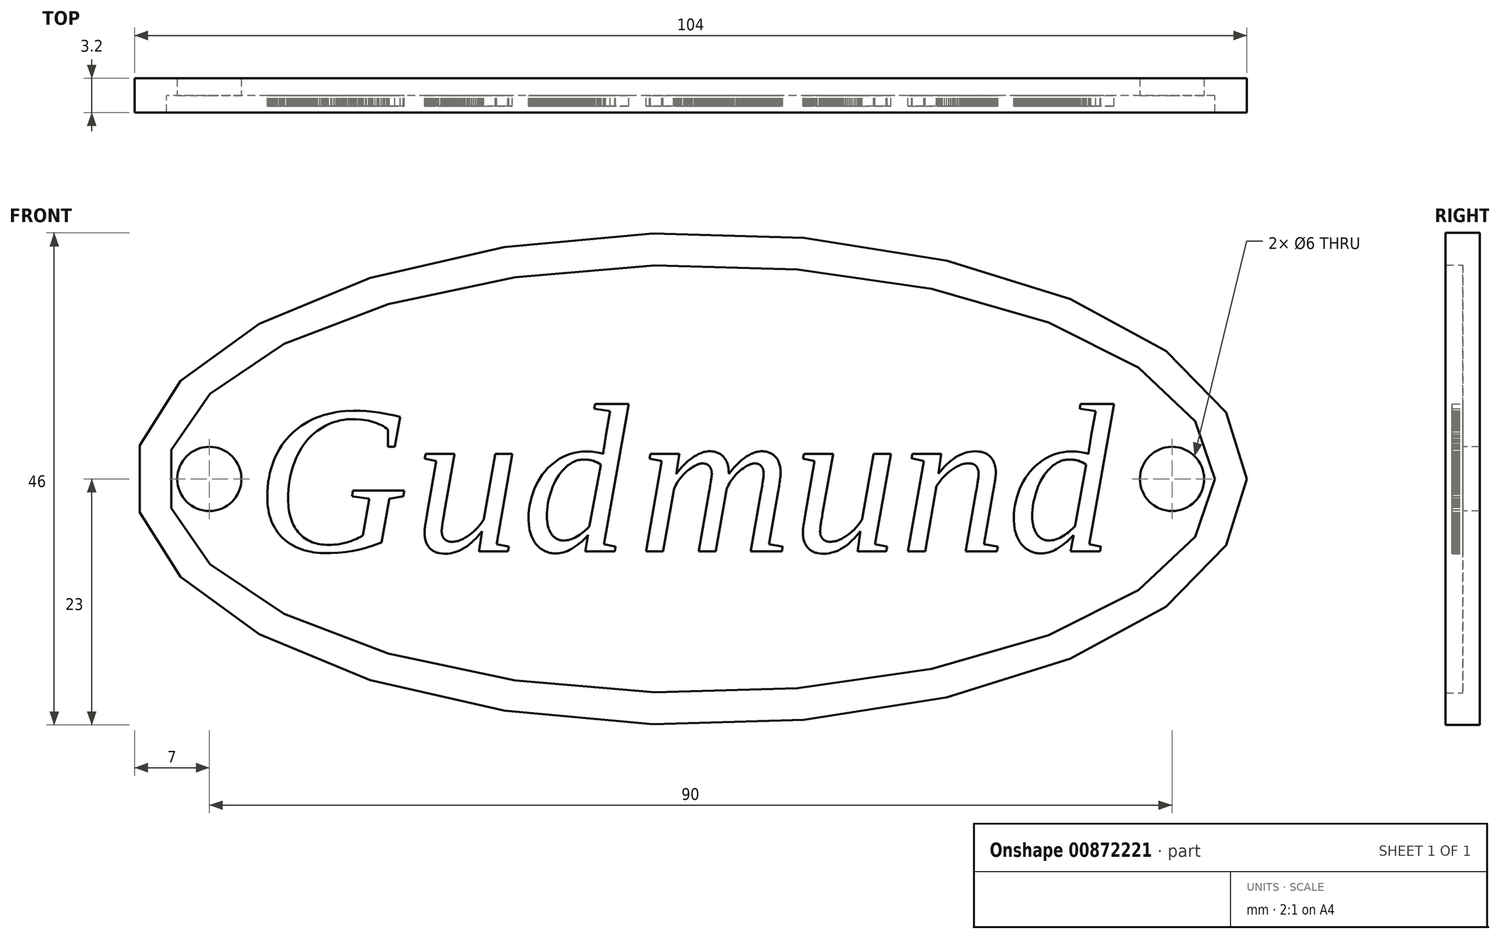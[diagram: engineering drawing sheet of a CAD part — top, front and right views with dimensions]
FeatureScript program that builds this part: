
annotation { "Feature Type Name" : "Feature", "Feature Type Description" : "" }
export const myFeature = defineFeature(function(context is Context, id is Id, definition is map)
    precondition{}
    {
        {
            var Q0;
            Q0=qCreatedBy(makeId("Front.planeOp"),FACE);
            var sketch = newSketch(context, id + "F0", { "sketchPlane" : qUnion([Q0])});
            skEllipse(sketch, "E0", {"center": v(0, 0) * mm, "majorRadius": 49 * mm, "minorRadius": 20 * mm, "majorAxis": v(1, 0)});
            skEllipse(sketch, "E1", {"center": v(0, 0) * mm, "majorRadius": 52 * mm, "minorRadius": 23 * mm, "majorAxis": v(1, 0)});
            skLineSegment(sketch, "E2", {"start": v(-81.12, 0) * mm, "end": v(85, 0) * mm, "construction": true});
            skPoint(sketch, "E2.startSnap0", {"position": v(-52, 0) * mm});
            skPoint(sketch, "E2.endSnap0", {"position": v(52, 0) * mm});
            skCircle(sketch, "E3", {"center": v(-45, 0) * mm, "radius": 3 * mm});
            skCircle(sketch, "E4", {"center": v(45, 0) * mm, "radius": 3 * mm});
            skLineSegment(sketch, "E5", {"start": v(-28.9, -5.93) * mm, "end": v(-29.2, -6.05) * mm});
            skLineSegment(sketch, "E6", {"start": v(-29.2, -6.05) * mm, "end": v(-29.8, -6.26) * mm});
            skLineSegment(sketch, "E7", {"start": v(-29.8, -6.26) * mm, "end": v(-30.1, -6.36) * mm});
            skLineSegment(sketch, "E8", {"start": v(-30.1, -6.36) * mm, "end": v(-30.4, -6.45) * mm});
            skLineSegment(sketch, "E9", {"start": v(-30.4, -6.45) * mm, "end": v(-31, -6.6) * mm});
            skLineSegment(sketch, "E10", {"start": v(-31, -6.6) * mm, "end": v(-31.3, -6.68) * mm});
            skLineSegment(sketch, "E11", {"start": v(-31.3, -6.68) * mm, "end": v(-31.62, -6.74) * mm});
            skLineSegment(sketch, "E12", {"start": v(-31.62, -6.74) * mm, "end": v(-32.26, -6.84) * mm});
            skLineSegment(sketch, "E13", {"start": v(-32.26, -6.84) * mm, "end": v(-32.6, -6.87) * mm});
            skLineSegment(sketch, "E14", {"start": v(-32.6, -6.87) * mm, "end": v(-32.93, -6.9) * mm});
            skLineSegment(sketch, "E15", {"start": v(-32.93, -6.9) * mm, "end": v(-33.63, -6.94) * mm});
            skLineSegment(sketch, "E16", {"start": v(-33.63, -6.94) * mm, "end": v(-33.99, -6.94) * mm});
            skLineSegment(sketch, "E17", {"start": v(-33.99, -6.94) * mm, "end": v(-34.32, -6.94) * mm});
            skLineSegment(sketch, "E18", {"start": v(-34.32, -6.94) * mm, "end": v(-34.64, -6.92) * mm});
            skLineSegment(sketch, "E19", {"start": v(-34.64, -6.92) * mm, "end": v(-34.95, -6.9) * mm});
            skLineSegment(sketch, "E20", {"start": v(-34.95, -6.9) * mm, "end": v(-35.25, -6.85) * mm});
            skLineSegment(sketch, "E21", {"start": v(-35.25, -6.85) * mm, "end": v(-35.55, -6.8) * mm});
            skLineSegment(sketch, "E22", {"start": v(-35.55, -6.8) * mm, "end": v(-35.83, -6.74) * mm});
            skLineSegment(sketch, "E23", {"start": v(-35.83, -6.74) * mm, "end": v(-36.1, -6.67) * mm});
            skLineSegment(sketch, "E24", {"start": v(-36.1, -6.67) * mm, "end": v(-36.37, -6.58) * mm});
            skLineSegment(sketch, "E25", {"start": v(-36.37, -6.58) * mm, "end": v(-36.63, -6.49) * mm});
            skLineSegment(sketch, "E26", {"start": v(-36.63, -6.49) * mm, "end": v(-36.87, -6.38) * mm});
            skLineSegment(sketch, "E27", {"start": v(-36.87, -6.38) * mm, "end": v(-37.1, -6.26) * mm});
            skLineSegment(sketch, "E28", {"start": v(-37.1, -6.26) * mm, "end": v(-37.33, -6.14) * mm});
            skLineSegment(sketch, "E29", {"start": v(-37.33, -6.14) * mm, "end": v(-37.54, -6) * mm});
            skLineSegment(sketch, "E30", {"start": v(-37.54, -6) * mm, "end": v(-37.75, -5.86) * mm});
            skLineSegment(sketch, "E31", {"start": v(-37.75, -5.86) * mm, "end": v(-37.94, -5.7) * mm});
            skLineSegment(sketch, "E32", {"start": v(-37.94, -5.7) * mm, "end": v(-38.13, -5.54) * mm});
            skLineSegment(sketch, "E33", {"start": v(-38.13, -5.54) * mm, "end": v(-38.3, -5.36) * mm});
            skLineSegment(sketch, "E34", {"start": v(-38.3, -5.36) * mm, "end": v(-38.46, -5.18) * mm});
            skLineSegment(sketch, "E35", {"start": v(-38.46, -5.18) * mm, "end": v(-38.61, -4.99) * mm});
            skLineSegment(sketch, "E36", {"start": v(-38.61, -4.99) * mm, "end": v(-38.75, -4.79) * mm});
            skLineSegment(sketch, "E37", {"start": v(-38.75, -4.79) * mm, "end": v(-38.88, -4.58) * mm});
            skLineSegment(sketch, "E38", {"start": v(-38.88, -4.58) * mm, "end": v(-39, -4.36) * mm});
            skLineSegment(sketch, "E39", {"start": v(-39, -4.36) * mm, "end": v(-39.11, -4.13) * mm});
            skLineSegment(sketch, "E40", {"start": v(-39.11, -4.13) * mm, "end": v(-39.21, -3.9) * mm});
            skLineSegment(sketch, "E41", {"start": v(-39.21, -3.9) * mm, "end": v(-39.3, -3.64) * mm});
            skLineSegment(sketch, "E42", {"start": v(-39.3, -3.64) * mm, "end": v(-39.37, -3.39) * mm});
            skLineSegment(sketch, "E43", {"start": v(-39.37, -3.39) * mm, "end": v(-39.44, -3.13) * mm});
            skLineSegment(sketch, "E44", {"start": v(-39.44, -3.13) * mm, "end": v(-39.49, -2.86) * mm});
            skLineSegment(sketch, "E45", {"start": v(-39.49, -2.86) * mm, "end": v(-39.53, -2.58) * mm});
            skLineSegment(sketch, "E46", {"start": v(-39.53, -2.58) * mm, "end": v(-39.56, -2.3) * mm});
            skLineSegment(sketch, "E47", {"start": v(-39.56, -2.3) * mm, "end": v(-39.57, -2) * mm});
            skLineSegment(sketch, "E48", {"start": v(-39.57, -2) * mm, "end": v(-39.58, -1.7) * mm});
            skLineSegment(sketch, "E49", {"start": v(-39.58, -1.7) * mm, "end": v(-39.57, -1.22) * mm});
            skLineSegment(sketch, "E50", {"start": v(-39.57, -1.22) * mm, "end": v(-39.54, -0.75) * mm});
            skLineSegment(sketch, "E51", {"start": v(-39.54, -0.75) * mm, "end": v(-39.5, -0.3) * mm});
            skLineSegment(sketch, "E52", {"start": v(-39.5, -0.3) * mm, "end": v(-39.42, 0.14) * mm});
            skLineSegment(sketch, "E53", {"start": v(-39.42, 0.14) * mm, "end": v(-39.34, 0.56) * mm});
            skLineSegment(sketch, "E54", {"start": v(-39.34, 0.56) * mm, "end": v(-39.23, 0.97) * mm});
            skLineSegment(sketch, "E55", {"start": v(-39.23, 0.97) * mm, "end": v(-39.1, 1.37) * mm});
            skLineSegment(sketch, "E56", {"start": v(-39.1, 1.37) * mm, "end": v(-38.96, 1.75) * mm});
            skLineSegment(sketch, "E57", {"start": v(-38.96, 1.75) * mm, "end": v(-38.8, 2.12) * mm});
            skLineSegment(sketch, "E58", {"start": v(-38.8, 2.12) * mm, "end": v(-38.62, 2.47) * mm});
            skLineSegment(sketch, "E59", {"start": v(-38.62, 2.47) * mm, "end": v(-38.43, 2.8) * mm});
            skLineSegment(sketch, "E60", {"start": v(-38.43, 2.8) * mm, "end": v(-38.22, 3.13) * mm});
            skLineSegment(sketch, "E61", {"start": v(-38.22, 3.13) * mm, "end": v(-38, 3.44) * mm});
            skLineSegment(sketch, "E62", {"start": v(-38, 3.44) * mm, "end": v(-37.77, 3.73) * mm});
            skLineSegment(sketch, "E63", {"start": v(-37.77, 3.73) * mm, "end": v(-37.52, 4.01) * mm});
            skLineSegment(sketch, "E64", {"start": v(-37.52, 4.01) * mm, "end": v(-37.25, 4.28) * mm});
            skLineSegment(sketch, "E65", {"start": v(-37.25, 4.28) * mm, "end": v(-36.98, 4.53) * mm});
            skLineSegment(sketch, "E66", {"start": v(-36.98, 4.53) * mm, "end": v(-36.69, 4.76) * mm});
            skLineSegment(sketch, "E67", {"start": v(-36.69, 4.76) * mm, "end": v(-36.39, 4.98) * mm});
            skLineSegment(sketch, "E68", {"start": v(-36.39, 4.98) * mm, "end": v(-36.07, 5.18) * mm});
            skLineSegment(sketch, "E69", {"start": v(-36.07, 5.18) * mm, "end": v(-35.75, 5.37) * mm});
            skLineSegment(sketch, "E70", {"start": v(-35.75, 5.37) * mm, "end": v(-35.4, 5.54) * mm});
            skLineSegment(sketch, "E71", {"start": v(-35.4, 5.54) * mm, "end": v(-35.06, 5.7) * mm});
            skLineSegment(sketch, "E72", {"start": v(-35.06, 5.7) * mm, "end": v(-34.7, 5.84) * mm});
            skLineSegment(sketch, "E73", {"start": v(-34.7, 5.84) * mm, "end": v(-34.32, 5.96) * mm});
            skLineSegment(sketch, "E74", {"start": v(-34.32, 5.96) * mm, "end": v(-33.94, 6.07) * mm});
            skLineSegment(sketch, "E75", {"start": v(-33.94, 6.07) * mm, "end": v(-33.55, 6.16) * mm});
            skLineSegment(sketch, "E76", {"start": v(-33.55, 6.16) * mm, "end": v(-33.16, 6.24) * mm});
            skLineSegment(sketch, "E77", {"start": v(-33.16, 6.24) * mm, "end": v(-32.75, 6.3) * mm});
            skLineSegment(sketch, "E78", {"start": v(-32.75, 6.3) * mm, "end": v(-32.34, 6.34) * mm});
            skLineSegment(sketch, "E79", {"start": v(-32.34, 6.34) * mm, "end": v(-31.5, 6.37) * mm});
            skLineSegment(sketch, "E80", {"start": v(-31.5, 6.37) * mm, "end": v(-30.89, 6.36) * mm});
            skLineSegment(sketch, "E81", {"start": v(-30.89, 6.36) * mm, "end": v(-30.3, 6.33) * mm});
            skLineSegment(sketch, "E82", {"start": v(-30.3, 6.33) * mm, "end": v(-29.74, 6.28) * mm});
            skLineSegment(sketch, "E83", {"start": v(-29.74, 6.28) * mm, "end": v(-29.2, 6.22) * mm});
            skLineSegment(sketch, "E84", {"start": v(-29.2, 6.22) * mm, "end": v(-28.68, 6.13) * mm});
            skLineSegment(sketch, "E85", {"start": v(-28.68, 6.13) * mm, "end": v(-27.66, 5.92) * mm});
            skLineSegment(sketch, "E86", {"start": v(-27.66, 5.92) * mm, "end": v(-27.17, 5.79) * mm});
            skLineSegment(sketch, "E87", {"start": v(-27.17, 5.79) * mm, "end": v(-27.66, 3) * mm});
            skLineSegment(sketch, "E88", {"start": v(-27.66, 3) * mm, "end": v(-28.31, 3) * mm});
            skLineSegment(sketch, "E89", {"start": v(-28.31, 3) * mm, "end": v(-28.28, 4.6) * mm});
            skLineSegment(sketch, "E90", {"start": v(-28.28, 4.6) * mm, "end": v(-28.43, 4.72) * mm});
            skLineSegment(sketch, "E91", {"start": v(-28.43, 4.72) * mm, "end": v(-28.6, 4.83) * mm});
            skLineSegment(sketch, "E92", {"start": v(-28.6, 4.83) * mm, "end": v(-28.76, 4.93) * mm});
            skLineSegment(sketch, "E93", {"start": v(-28.76, 4.93) * mm, "end": v(-28.93, 5.03) * mm});
            skLineSegment(sketch, "E94", {"start": v(-28.93, 5.03) * mm, "end": v(-29.11, 5.11) * mm});
            skLineSegment(sketch, "E95", {"start": v(-29.11, 5.11) * mm, "end": v(-29.3, 5.2) * mm});
            skLineSegment(sketch, "E96", {"start": v(-29.3, 5.2) * mm, "end": v(-29.5, 5.27) * mm});
            skLineSegment(sketch, "E97", {"start": v(-29.5, 5.27) * mm, "end": v(-29.7, 5.33) * mm});
            skLineSegment(sketch, "E98", {"start": v(-29.7, 5.33) * mm, "end": v(-29.9, 5.4) * mm});
            skLineSegment(sketch, "E99", {"start": v(-29.9, 5.4) * mm, "end": v(-30.12, 5.45) * mm});
            skLineSegment(sketch, "E100", {"start": v(-30.12, 5.45) * mm, "end": v(-30.34, 5.5) * mm});
            skLineSegment(sketch, "E101", {"start": v(-30.34, 5.5) * mm, "end": v(-30.57, 5.53) * mm});
            skLineSegment(sketch, "E102", {"start": v(-30.57, 5.53) * mm, "end": v(-30.8, 5.56) * mm});
            skLineSegment(sketch, "E103", {"start": v(-30.8, 5.56) * mm, "end": v(-31.3, 5.6) * mm});
            skLineSegment(sketch, "E104", {"start": v(-31.3, 5.6) * mm, "end": v(-31.56, 5.6) * mm});
            skLineSegment(sketch, "E105", {"start": v(-31.56, 5.6) * mm, "end": v(-31.86, 5.59) * mm});
            skLineSegment(sketch, "E106", {"start": v(-31.86, 5.59) * mm, "end": v(-32.16, 5.56) * mm});
            skLineSegment(sketch, "E107", {"start": v(-32.16, 5.56) * mm, "end": v(-32.45, 5.53) * mm});
            skLineSegment(sketch, "E108", {"start": v(-32.45, 5.53) * mm, "end": v(-32.74, 5.47) * mm});
            skLineSegment(sketch, "E109", {"start": v(-32.74, 5.47) * mm, "end": v(-33.03, 5.4) * mm});
            skLineSegment(sketch, "E110", {"start": v(-33.03, 5.4) * mm, "end": v(-33.31, 5.32) * mm});
            skLineSegment(sketch, "E111", {"start": v(-33.31, 5.32) * mm, "end": v(-33.6, 5.22) * mm});
            skLineSegment(sketch, "E112", {"start": v(-33.6, 5.22) * mm, "end": v(-33.87, 5.1) * mm});
            skLineSegment(sketch, "E113", {"start": v(-33.87, 5.1) * mm, "end": v(-34.14, 4.97) * mm});
            skLineSegment(sketch, "E114", {"start": v(-34.14, 4.97) * mm, "end": v(-34.4, 4.83) * mm});
            skLineSegment(sketch, "E115", {"start": v(-34.4, 4.83) * mm, "end": v(-34.66, 4.67) * mm});
            skLineSegment(sketch, "E116", {"start": v(-34.66, 4.67) * mm, "end": v(-34.9, 4.5) * mm});
            skLineSegment(sketch, "E117", {"start": v(-34.9, 4.5) * mm, "end": v(-35.15, 4.31) * mm});
            skLineSegment(sketch, "E118", {"start": v(-35.15, 4.31) * mm, "end": v(-35.38, 4.11) * mm});
            skLineSegment(sketch, "E119", {"start": v(-35.38, 4.11) * mm, "end": v(-35.6, 3.9) * mm});
            skLineSegment(sketch, "E120", {"start": v(-35.6, 3.9) * mm, "end": v(-35.81, 3.67) * mm});
            skLineSegment(sketch, "E121", {"start": v(-35.81, 3.67) * mm, "end": v(-36.01, 3.42) * mm});
            skLineSegment(sketch, "E122", {"start": v(-36.01, 3.42) * mm, "end": v(-36.2, 3.16) * mm});
            skLineSegment(sketch, "E123", {"start": v(-36.2, 3.16) * mm, "end": v(-36.39, 2.9) * mm});
            skLineSegment(sketch, "E124", {"start": v(-36.39, 2.9) * mm, "end": v(-36.56, 2.6) * mm});
            skLineSegment(sketch, "E125", {"start": v(-36.56, 2.6) * mm, "end": v(-36.72, 2.3) * mm});
            skLineSegment(sketch, "E126", {"start": v(-36.72, 2.3) * mm, "end": v(-36.87, 1.99) * mm});
            skLineSegment(sketch, "E127", {"start": v(-36.87, 1.99) * mm, "end": v(-37, 1.66) * mm});
            skLineSegment(sketch, "E128", {"start": v(-37, 1.66) * mm, "end": v(-37.14, 1.31) * mm});
            skLineSegment(sketch, "E129", {"start": v(-37.14, 1.31) * mm, "end": v(-37.25, 0.96) * mm});
            skLineSegment(sketch, "E130", {"start": v(-37.25, 0.96) * mm, "end": v(-37.35, 0.59) * mm});
            skLineSegment(sketch, "E131", {"start": v(-37.35, 0.59) * mm, "end": v(-37.44, 0.2) * mm});
            skLineSegment(sketch, "E132", {"start": v(-37.44, 0.2) * mm, "end": v(-37.5, -0.19) * mm});
            skLineSegment(sketch, "E133", {"start": v(-37.5, -0.19) * mm, "end": v(-37.56, -0.6) * mm});
            skLineSegment(sketch, "E134", {"start": v(-37.56, -0.6) * mm, "end": v(-37.6, -1.01) * mm});
            skLineSegment(sketch, "E135", {"start": v(-37.6, -1.01) * mm, "end": v(-37.62, -1.45) * mm});
            skLineSegment(sketch, "E136", {"start": v(-37.62, -1.45) * mm, "end": v(-37.63, -1.9) * mm});
            skLineSegment(sketch, "E137", {"start": v(-37.63, -1.9) * mm, "end": v(-37.63, -2.16) * mm});
            skLineSegment(sketch, "E138", {"start": v(-37.63, -2.16) * mm, "end": v(-37.61, -2.41) * mm});
            skLineSegment(sketch, "E139", {"start": v(-37.61, -2.41) * mm, "end": v(-37.6, -2.66) * mm});
            skLineSegment(sketch, "E140", {"start": v(-37.6, -2.66) * mm, "end": v(-37.56, -2.9) * mm});
            skLineSegment(sketch, "E141", {"start": v(-37.56, -2.9) * mm, "end": v(-37.53, -3.12) * mm});
            skLineSegment(sketch, "E142", {"start": v(-37.53, -3.12) * mm, "end": v(-37.48, -3.35) * mm});
            skLineSegment(sketch, "E143", {"start": v(-37.48, -3.35) * mm, "end": v(-37.42, -3.56) * mm});
            skLineSegment(sketch, "E144", {"start": v(-37.42, -3.56) * mm, "end": v(-37.36, -3.76) * mm});
            skLineSegment(sketch, "E145", {"start": v(-37.36, -3.76) * mm, "end": v(-37.29, -3.96) * mm});
            skLineSegment(sketch, "E146", {"start": v(-37.29, -3.96) * mm, "end": v(-37.2, -4.15) * mm});
            skLineSegment(sketch, "E147", {"start": v(-37.2, -4.15) * mm, "end": v(-37.12, -4.33) * mm});
            skLineSegment(sketch, "E148", {"start": v(-37.12, -4.33) * mm, "end": v(-37.03, -4.5) * mm});
            skLineSegment(sketch, "E149", {"start": v(-37.03, -4.5) * mm, "end": v(-36.93, -4.66) * mm});
            skLineSegment(sketch, "E150", {"start": v(-36.93, -4.66) * mm, "end": v(-36.82, -4.82) * mm});
            skLineSegment(sketch, "E151", {"start": v(-36.82, -4.82) * mm, "end": v(-36.7, -4.96) * mm});
            skLineSegment(sketch, "E152", {"start": v(-36.7, -4.96) * mm, "end": v(-36.59, -5.1) * mm});
            skLineSegment(sketch, "E153", {"start": v(-36.59, -5.1) * mm, "end": v(-36.46, -5.23) * mm});
            skLineSegment(sketch, "E154", {"start": v(-36.46, -5.23) * mm, "end": v(-36.33, -5.35) * mm});
            skLineSegment(sketch, "E155", {"start": v(-36.33, -5.35) * mm, "end": v(-36.19, -5.46) * mm});
            skLineSegment(sketch, "E156", {"start": v(-36.19, -5.46) * mm, "end": v(-36.04, -5.57) * mm});
            skLineSegment(sketch, "E157", {"start": v(-36.04, -5.57) * mm, "end": v(-35.9, -5.67) * mm});
            skLineSegment(sketch, "E158", {"start": v(-35.9, -5.67) * mm, "end": v(-35.74, -5.75) * mm});
            skLineSegment(sketch, "E159", {"start": v(-35.74, -5.75) * mm, "end": v(-35.57, -5.83) * mm});
            skLineSegment(sketch, "E160", {"start": v(-35.57, -5.83) * mm, "end": v(-35.4, -5.9) * mm});
            skLineSegment(sketch, "E161", {"start": v(-35.4, -5.9) * mm, "end": v(-35.23, -5.97) * mm});
            skLineSegment(sketch, "E162", {"start": v(-35.23, -5.97) * mm, "end": v(-35.05, -6.02) * mm});
            skLineSegment(sketch, "E163", {"start": v(-35.05, -6.02) * mm, "end": v(-34.86, -6.06) * mm});
            skLineSegment(sketch, "E164", {"start": v(-34.86, -6.06) * mm, "end": v(-34.67, -6.1) * mm});
            skLineSegment(sketch, "E165", {"start": v(-34.67, -6.1) * mm, "end": v(-34.47, -6.13) * mm});
            skLineSegment(sketch, "E166", {"start": v(-34.47, -6.13) * mm, "end": v(-34.28, -6.15) * mm});
            skLineSegment(sketch, "E167", {"start": v(-34.28, -6.15) * mm, "end": v(-34.07, -6.16) * mm});
            skLineSegment(sketch, "E168", {"start": v(-34.07, -6.16) * mm, "end": v(-33.86, -6.17) * mm});
            skLineSegment(sketch, "E169", {"start": v(-33.86, -6.17) * mm, "end": v(-33.6, -6.16) * mm});
            skLineSegment(sketch, "E170", {"start": v(-33.6, -6.16) * mm, "end": v(-33.35, -6.15) * mm});
            skLineSegment(sketch, "E171", {"start": v(-33.35, -6.15) * mm, "end": v(-33.1, -6.12) * mm});
            skLineSegment(sketch, "E172", {"start": v(-33.1, -6.12) * mm, "end": v(-32.87, -6.09) * mm});
            skLineSegment(sketch, "E173", {"start": v(-32.87, -6.09) * mm, "end": v(-32.63, -6.04) * mm});
            skLineSegment(sketch, "E174", {"start": v(-32.63, -6.04) * mm, "end": v(-32.19, -5.94) * mm});
            skLineSegment(sketch, "E175", {"start": v(-32.19, -5.94) * mm, "end": v(-31.97, -5.88) * mm});
            skLineSegment(sketch, "E176", {"start": v(-31.97, -5.88) * mm, "end": v(-31.77, -5.8) * mm});
            skLineSegment(sketch, "E177", {"start": v(-31.77, -5.8) * mm, "end": v(-31.58, -5.74) * mm});
            skLineSegment(sketch, "E178", {"start": v(-31.58, -5.74) * mm, "end": v(-31.4, -5.66) * mm});
            skLineSegment(sketch, "E179", {"start": v(-31.4, -5.66) * mm, "end": v(-31.22, -5.59) * mm});
            skLineSegment(sketch, "E180", {"start": v(-31.22, -5.59) * mm, "end": v(-31.06, -5.5) * mm});
            skLineSegment(sketch, "E181", {"start": v(-31.06, -5.5) * mm, "end": v(-30.9, -5.43) * mm});
            skLineSegment(sketch, "E182", {"start": v(-30.9, -5.43) * mm, "end": v(-30.77, -5.36) * mm});
            skLineSegment(sketch, "E183", {"start": v(-30.77, -5.36) * mm, "end": v(-30.7, -5.32) * mm});
            skLineSegment(sketch, "E184", {"start": v(-30.7, -5.32) * mm, "end": v(-30.65, -5.29) * mm});
            skLineSegment(sketch, "E185", {"start": v(-30.65, -5.29) * mm, "end": v(-30.04, -1.87) * mm});
            skLineSegment(sketch, "E186", {"start": v(-30.04, -1.87) * mm, "end": v(-31.65, -1.61) * mm});
            skLineSegment(sketch, "E187", {"start": v(-31.65, -1.61) * mm, "end": v(-31.57, -1.09) * mm});
            skLineSegment(sketch, "E188", {"start": v(-31.57, -1.09) * mm, "end": v(-26.77, -1.09) * mm});
            skLineSegment(sketch, "E189", {"start": v(-26.77, -1.09) * mm, "end": v(-26.86, -1.61) * mm});
            skLineSegment(sketch, "E190", {"start": v(-26.86, -1.61) * mm, "end": v(-28.18, -1.87) * mm});
            skLineSegment(sketch, "E191", {"start": v(-28.18, -1.87) * mm, "end": v(-28.9, -5.93) * mm});
            skLineSegment(sketch, "E192", {"start": v(-23.27, -4.9) * mm, "end": v(-23.27, -5) * mm});
            skLineSegment(sketch, "E193", {"start": v(-23.27, -5) * mm, "end": v(-23.26, -5.06) * mm});
            skLineSegment(sketch, "E194", {"start": v(-23.26, -5.06) * mm, "end": v(-23.26, -5.1) * mm});
            skLineSegment(sketch, "E195", {"start": v(-23.26, -5.1) * mm, "end": v(-23.25, -5.15) * mm});
            skLineSegment(sketch, "E196", {"start": v(-23.25, -5.15) * mm, "end": v(-23.24, -5.2) * mm});
            skLineSegment(sketch, "E197", {"start": v(-23.24, -5.2) * mm, "end": v(-23.23, -5.25) * mm});
            skLineSegment(sketch, "E198", {"start": v(-23.23, -5.25) * mm, "end": v(-23.21, -5.3) * mm});
            skLineSegment(sketch, "E199", {"start": v(-23.21, -5.3) * mm, "end": v(-23.2, -5.34) * mm});
            skLineSegment(sketch, "E200", {"start": v(-23.2, -5.34) * mm, "end": v(-23.18, -5.38) * mm});
            skLineSegment(sketch, "E201", {"start": v(-23.18, -5.38) * mm, "end": v(-23.16, -5.42) * mm});
            skLineSegment(sketch, "E202", {"start": v(-23.16, -5.42) * mm, "end": v(-23.14, -5.46) * mm});
            skLineSegment(sketch, "E203", {"start": v(-23.14, -5.46) * mm, "end": v(-23.12, -5.5) * mm});
            skLineSegment(sketch, "E204", {"start": v(-23.12, -5.5) * mm, "end": v(-23.1, -5.53) * mm});
            skLineSegment(sketch, "E205", {"start": v(-23.1, -5.53) * mm, "end": v(-23.07, -5.57) * mm});
            skLineSegment(sketch, "E206", {"start": v(-23.07, -5.57) * mm, "end": v(-23.04, -5.6) * mm});
            skLineSegment(sketch, "E207", {"start": v(-23.04, -5.6) * mm, "end": v(-23.01, -5.64) * mm});
            skLineSegment(sketch, "E208", {"start": v(-23.01, -5.64) * mm, "end": v(-22.98, -5.67) * mm});
            skLineSegment(sketch, "E209", {"start": v(-22.98, -5.67) * mm, "end": v(-22.94, -5.7) * mm});
            skLineSegment(sketch, "E210", {"start": v(-22.94, -5.7) * mm, "end": v(-22.9, -5.72) * mm});
            skLineSegment(sketch, "E211", {"start": v(-22.9, -5.72) * mm, "end": v(-22.87, -5.75) * mm});
            skLineSegment(sketch, "E212", {"start": v(-22.87, -5.75) * mm, "end": v(-22.83, -5.77) * mm});
            skLineSegment(sketch, "E213", {"start": v(-22.83, -5.77) * mm, "end": v(-22.79, -5.8) * mm});
            skLineSegment(sketch, "E214", {"start": v(-22.79, -5.8) * mm, "end": v(-22.74, -5.8) * mm});
            skLineSegment(sketch, "E215", {"start": v(-22.74, -5.8) * mm, "end": v(-22.7, -5.82) * mm});
            skLineSegment(sketch, "E216", {"start": v(-22.7, -5.82) * mm, "end": v(-22.64, -5.84) * mm});
            skLineSegment(sketch, "E217", {"start": v(-22.64, -5.84) * mm, "end": v(-22.6, -5.85) * mm});
            skLineSegment(sketch, "E218", {"start": v(-22.6, -5.85) * mm, "end": v(-22.54, -5.86) * mm});
            skLineSegment(sketch, "E219", {"start": v(-22.54, -5.86) * mm, "end": v(-22.48, -5.87) * mm});
            skLineSegment(sketch, "E220", {"start": v(-22.48, -5.87) * mm, "end": v(-22.43, -5.87) * mm});
            skLineSegment(sketch, "E221", {"start": v(-22.43, -5.87) * mm, "end": v(-22.37, -5.88) * mm});
            skLineSegment(sketch, "E222", {"start": v(-22.37, -5.88) * mm, "end": v(-22.3, -5.88) * mm});
            skLineSegment(sketch, "E223", {"start": v(-22.3, -5.88) * mm, "end": v(-22.2, -5.87) * mm});
            skLineSegment(sketch, "E224", {"start": v(-22.2, -5.87) * mm, "end": v(-22.1, -5.86) * mm});
            skLineSegment(sketch, "E225", {"start": v(-22.1, -5.86) * mm, "end": v(-22, -5.85) * mm});
            skLineSegment(sketch, "E226", {"start": v(-22, -5.85) * mm, "end": v(-21.9, -5.83) * mm});
            skLineSegment(sketch, "E227", {"start": v(-21.9, -5.83) * mm, "end": v(-21.79, -5.8) * mm});
            skLineSegment(sketch, "E228", {"start": v(-21.79, -5.8) * mm, "end": v(-21.68, -5.77) * mm});
            skLineSegment(sketch, "E229", {"start": v(-21.68, -5.77) * mm, "end": v(-21.58, -5.74) * mm});
            skLineSegment(sketch, "E230", {"start": v(-21.58, -5.74) * mm, "end": v(-21.47, -5.7) * mm});
            skLineSegment(sketch, "E231", {"start": v(-21.47, -5.7) * mm, "end": v(-21.26, -5.6) * mm});
            skLineSegment(sketch, "E232", {"start": v(-21.26, -5.6) * mm, "end": v(-21.05, -5.48) * mm});
            skLineSegment(sketch, "E233", {"start": v(-21.05, -5.48) * mm, "end": v(-20.85, -5.36) * mm});
            skLineSegment(sketch, "E234", {"start": v(-20.85, -5.36) * mm, "end": v(-20.66, -5.22) * mm});
            skLineSegment(sketch, "E235", {"start": v(-20.66, -5.22) * mm, "end": v(-20.46, -5.06) * mm});
            skLineSegment(sketch, "E236", {"start": v(-20.46, -5.06) * mm, "end": v(-20.27, -4.9) * mm});
            skLineSegment(sketch, "E237", {"start": v(-20.27, -4.9) * mm, "end": v(-20.1, -4.72) * mm});
            skLineSegment(sketch, "E238", {"start": v(-20.1, -4.72) * mm, "end": v(-19.92, -4.54) * mm});
            skLineSegment(sketch, "E239", {"start": v(-19.92, -4.54) * mm, "end": v(-19.76, -4.35) * mm});
            skLineSegment(sketch, "E240", {"start": v(-19.76, -4.35) * mm, "end": v(-19.6, -4.16) * mm});
            skLineSegment(sketch, "E241", {"start": v(-19.6, -4.16) * mm, "end": v(-19.47, -3.97) * mm});
            skLineSegment(sketch, "E242", {"start": v(-19.47, -3.97) * mm, "end": v(-19.35, -3.78) * mm});
            skLineSegment(sketch, "E243", {"start": v(-19.35, -3.78) * mm, "end": v(-18.27, 2.34) * mm});
            skLineSegment(sketch, "E244", {"start": v(-18.27, 2.34) * mm, "end": v(-16.67, 2.34) * mm});
            skLineSegment(sketch, "E245", {"start": v(-16.67, 2.34) * mm, "end": v(-18.15, -6.09) * mm});
            skLineSegment(sketch, "E246", {"start": v(-18.15, -6.09) * mm, "end": v(-17, -6.33) * mm});
            skLineSegment(sketch, "E247", {"start": v(-17, -6.33) * mm, "end": v(-17.08, -6.77) * mm});
            skLineSegment(sketch, "E248", {"start": v(-17.08, -6.77) * mm, "end": v(-19.78, -6.77) * mm});
            skLineSegment(sketch, "E249", {"start": v(-19.78, -6.77) * mm, "end": v(-19.51, -4.9) * mm});
            skLineSegment(sketch, "E250", {"start": v(-19.51, -4.9) * mm, "end": v(-19.7, -5.13) * mm});
            skLineSegment(sketch, "E251", {"start": v(-19.7, -5.13) * mm, "end": v(-20.09, -5.56) * mm});
            skLineSegment(sketch, "E252", {"start": v(-20.09, -5.56) * mm, "end": v(-20.29, -5.76) * mm});
            skLineSegment(sketch, "E253", {"start": v(-20.29, -5.76) * mm, "end": v(-20.49, -5.95) * mm});
            skLineSegment(sketch, "E254", {"start": v(-20.49, -5.95) * mm, "end": v(-20.7, -6.12) * mm});
            skLineSegment(sketch, "E255", {"start": v(-20.7, -6.12) * mm, "end": v(-20.9, -6.28) * mm});
            skLineSegment(sketch, "E256", {"start": v(-20.9, -6.28) * mm, "end": v(-21.12, -6.43) * mm});
            skLineSegment(sketch, "E257", {"start": v(-21.12, -6.43) * mm, "end": v(-21.34, -6.56) * mm});
            skLineSegment(sketch, "E258", {"start": v(-21.34, -6.56) * mm, "end": v(-21.56, -6.67) * mm});
            skLineSegment(sketch, "E259", {"start": v(-21.56, -6.67) * mm, "end": v(-21.78, -6.76) * mm});
            skLineSegment(sketch, "E260", {"start": v(-21.78, -6.76) * mm, "end": v(-22, -6.84) * mm});
            skLineSegment(sketch, "E261", {"start": v(-22, -6.84) * mm, "end": v(-22.23, -6.91) * mm});
            skLineSegment(sketch, "E262", {"start": v(-22.23, -6.91) * mm, "end": v(-22.45, -6.96) * mm});
            skLineSegment(sketch, "E263", {"start": v(-22.45, -6.96) * mm, "end": v(-22.68, -7) * mm});
            skLineSegment(sketch, "E264", {"start": v(-22.68, -7) * mm, "end": v(-22.91, -7) * mm});
            skLineSegment(sketch, "E265", {"start": v(-22.91, -7) * mm, "end": v(-23.13, -7) * mm});
            skLineSegment(sketch, "E266", {"start": v(-23.13, -7) * mm, "end": v(-23.34, -6.97) * mm});
            skLineSegment(sketch, "E267", {"start": v(-23.34, -6.97) * mm, "end": v(-23.54, -6.93) * mm});
            skLineSegment(sketch, "E268", {"start": v(-23.54, -6.93) * mm, "end": v(-23.64, -6.91) * mm});
            skLineSegment(sketch, "E269", {"start": v(-23.64, -6.91) * mm, "end": v(-23.73, -6.88) * mm});
            skLineSegment(sketch, "E270", {"start": v(-23.73, -6.88) * mm, "end": v(-23.82, -6.85) * mm});
            skLineSegment(sketch, "E271", {"start": v(-23.82, -6.85) * mm, "end": v(-23.9, -6.82) * mm});
            skLineSegment(sketch, "E272", {"start": v(-23.9, -6.82) * mm, "end": v(-23.98, -6.78) * mm});
            skLineSegment(sketch, "E273", {"start": v(-23.98, -6.78) * mm, "end": v(-24.06, -6.73) * mm});
            skLineSegment(sketch, "E274", {"start": v(-24.06, -6.73) * mm, "end": v(-24.14, -6.69) * mm});
            skLineSegment(sketch, "E275", {"start": v(-24.14, -6.69) * mm, "end": v(-24.21, -6.63) * mm});
            skLineSegment(sketch, "E276", {"start": v(-24.21, -6.63) * mm, "end": v(-24.28, -6.58) * mm});
            skLineSegment(sketch, "E277", {"start": v(-24.28, -6.58) * mm, "end": v(-24.35, -6.52) * mm});
            skLineSegment(sketch, "E278", {"start": v(-24.35, -6.52) * mm, "end": v(-24.4, -6.45) * mm});
            skLineSegment(sketch, "E279", {"start": v(-24.4, -6.45) * mm, "end": v(-24.47, -6.38) * mm});
            skLineSegment(sketch, "E280", {"start": v(-24.47, -6.38) * mm, "end": v(-24.52, -6.3) * mm});
            skLineSegment(sketch, "E281", {"start": v(-24.52, -6.3) * mm, "end": v(-24.57, -6.23) * mm});
            skLineSegment(sketch, "E282", {"start": v(-24.57, -6.23) * mm, "end": v(-24.62, -6.15) * mm});
            skLineSegment(sketch, "E283", {"start": v(-24.62, -6.15) * mm, "end": v(-24.67, -6.07) * mm});
            skLineSegment(sketch, "E284", {"start": v(-24.67, -6.07) * mm, "end": v(-24.7, -5.98) * mm});
            skLineSegment(sketch, "E285", {"start": v(-24.7, -5.98) * mm, "end": v(-24.75, -5.89) * mm});
            skLineSegment(sketch, "E286", {"start": v(-24.75, -5.89) * mm, "end": v(-24.78, -5.79) * mm});
            skLineSegment(sketch, "E287", {"start": v(-24.78, -5.79) * mm, "end": v(-24.8, -5.68) * mm});
            skLineSegment(sketch, "E288", {"start": v(-24.8, -5.68) * mm, "end": v(-24.83, -5.57) * mm});
            skLineSegment(sketch, "E289", {"start": v(-24.83, -5.57) * mm, "end": v(-24.85, -5.46) * mm});
            skLineSegment(sketch, "E290", {"start": v(-24.85, -5.46) * mm, "end": v(-24.86, -5.34) * mm});
            skLineSegment(sketch, "E291", {"start": v(-24.86, -5.34) * mm, "end": v(-24.87, -5.22) * mm});
            skLineSegment(sketch, "E292", {"start": v(-24.87, -5.22) * mm, "end": v(-24.88, -5.09) * mm});
            skLineSegment(sketch, "E293", {"start": v(-24.88, -5.09) * mm, "end": v(-24.88, -4.96) * mm});
            skLineSegment(sketch, "E294", {"start": v(-24.88, -4.96) * mm, "end": v(-24.88, -4.93) * mm});
            skLineSegment(sketch, "E295", {"start": v(-24.88, -4.93) * mm, "end": v(-24.88, -4.9) * mm});
            skLineSegment(sketch, "E296", {"start": v(-24.88, -4.9) * mm, "end": v(-24.88, -4.86) * mm});
            skLineSegment(sketch, "E297", {"start": v(-24.88, -4.86) * mm, "end": v(-24.88, -4.82) * mm});
            skLineSegment(sketch, "E298", {"start": v(-24.88, -4.82) * mm, "end": v(-24.87, -4.78) * mm});
            skLineSegment(sketch, "E299", {"start": v(-24.87, -4.78) * mm, "end": v(-24.87, -4.74) * mm});
            skLineSegment(sketch, "E300", {"start": v(-24.87, -4.74) * mm, "end": v(-24.87, -4.7) * mm});
            skLineSegment(sketch, "E301", {"start": v(-24.87, -4.7) * mm, "end": v(-24.86, -4.65) * mm});
            skLineSegment(sketch, "E302", {"start": v(-24.86, -4.65) * mm, "end": v(-24.85, -4.55) * mm});
            skLineSegment(sketch, "E303", {"start": v(-24.85, -4.55) * mm, "end": v(-24.83, -4.44) * mm});
            skLineSegment(sketch, "E304", {"start": v(-24.83, -4.44) * mm, "end": v(-24.8, -4.22) * mm});
            skLineSegment(sketch, "E305", {"start": v(-24.8, -4.22) * mm, "end": v(-24.78, -4.1) * mm});
            skLineSegment(sketch, "E306", {"start": v(-24.78, -4.1) * mm, "end": v(-24.75, -3.87) * mm});
            skLineSegment(sketch, "E307", {"start": v(-24.75, -3.87) * mm, "end": v(-24.73, -3.74) * mm});
            skLineSegment(sketch, "E308", {"start": v(-24.73, -3.74) * mm, "end": v(-24.7, -3.62) * mm});
            skLineSegment(sketch, "E309", {"start": v(-24.7, -3.62) * mm, "end": v(-24.66, -3.38) * mm});
            skLineSegment(sketch, "E310", {"start": v(-24.66, -3.38) * mm, "end": v(-24.64, -3.27) * mm});
            skLineSegment(sketch, "E311", {"start": v(-24.64, -3.27) * mm, "end": v(-23.79, 1.67) * mm});
            skLineSegment(sketch, "E312", {"start": v(-23.79, 1.67) * mm, "end": v(-24.86, 1.9) * mm});
            skLineSegment(sketch, "E313", {"start": v(-24.86, 1.9) * mm, "end": v(-24.78, 2.34) * mm});
            skLineSegment(sketch, "E314", {"start": v(-24.78, 2.34) * mm, "end": v(-22.06, 2.34) * mm});
            skLineSegment(sketch, "E315", {"start": v(-22.06, 2.34) * mm, "end": v(-23.05, -3.29) * mm});
            skLineSegment(sketch, "E316", {"start": v(-23.05, -3.29) * mm, "end": v(-23.07, -3.4) * mm});
            skLineSegment(sketch, "E317", {"start": v(-23.07, -3.4) * mm, "end": v(-23.1, -3.62) * mm});
            skLineSegment(sketch, "E318", {"start": v(-23.1, -3.62) * mm, "end": v(-23.13, -3.73) * mm});
            skLineSegment(sketch, "E319", {"start": v(-23.13, -3.73) * mm, "end": v(-23.15, -3.85) * mm});
            skLineSegment(sketch, "E320", {"start": v(-23.15, -3.85) * mm, "end": v(-23.19, -4.08) * mm});
            skLineSegment(sketch, "E321", {"start": v(-23.19, -4.08) * mm, "end": v(-23.2, -4.2) * mm});
            skLineSegment(sketch, "E322", {"start": v(-23.2, -4.2) * mm, "end": v(-23.22, -4.3) * mm});
            skLineSegment(sketch, "E323", {"start": v(-23.22, -4.3) * mm, "end": v(-23.23, -4.4) * mm});
            skLineSegment(sketch, "E324", {"start": v(-23.23, -4.4) * mm, "end": v(-23.24, -4.5) * mm});
            skLineSegment(sketch, "E325", {"start": v(-23.24, -4.5) * mm, "end": v(-23.25, -4.6) * mm});
            skLineSegment(sketch, "E326", {"start": v(-23.25, -4.6) * mm, "end": v(-23.26, -4.64) * mm});
            skLineSegment(sketch, "E327", {"start": v(-23.26, -4.64) * mm, "end": v(-23.26, -4.69) * mm});
            skLineSegment(sketch, "E328", {"start": v(-23.26, -4.69) * mm, "end": v(-23.27, -4.73) * mm});
            skLineSegment(sketch, "E329", {"start": v(-23.27, -4.73) * mm, "end": v(-23.27, -4.76) * mm});
            skLineSegment(sketch, "E330", {"start": v(-23.27, -4.76) * mm, "end": v(-23.27, -4.8) * mm});
            skLineSegment(sketch, "E331", {"start": v(-23.27, -4.8) * mm, "end": v(-23.27, -4.84) * mm});
            skLineSegment(sketch, "E332", {"start": v(-23.27, -4.84) * mm, "end": v(-23.27, -4.87) * mm});
            skLineSegment(sketch, "E333", {"start": v(-23.27, -4.87) * mm, "end": v(-23.27, -4.9) * mm});
            skLineSegment(sketch, "E334", {"start": v(-8.18, 2.35) * mm, "end": v(-8.18, 2.36) * mm});
            skLineSegment(sketch, "E335", {"start": v(-8.18, 2.36) * mm, "end": v(-8.17, 2.38) * mm});
            skLineSegment(sketch, "E336", {"start": v(-8.17, 2.38) * mm, "end": v(-8.17, 2.4) * mm});
            skLineSegment(sketch, "E337", {"start": v(-8.17, 2.4) * mm, "end": v(-8.17, 2.41) * mm});
            skLineSegment(sketch, "E338", {"start": v(-8.17, 2.41) * mm, "end": v(-8.17, 2.45) * mm});
            skLineSegment(sketch, "E339", {"start": v(-8.17, 2.45) * mm, "end": v(-8.16, 2.49) * mm});
            skLineSegment(sketch, "E340", {"start": v(-8.16, 2.49) * mm, "end": v(-8.16, 2.53) * mm});
            skLineSegment(sketch, "E341", {"start": v(-8.16, 2.53) * mm, "end": v(-8.15, 2.58) * mm});
            skLineSegment(sketch, "E342", {"start": v(-8.15, 2.58) * mm, "end": v(-8.15, 2.63) * mm});
            skLineSegment(sketch, "E343", {"start": v(-8.15, 2.63) * mm, "end": v(-8.14, 2.68) * mm});
            skLineSegment(sketch, "E344", {"start": v(-8.14, 2.68) * mm, "end": v(-8.12, 2.8) * mm});
            skLineSegment(sketch, "E345", {"start": v(-8.12, 2.8) * mm, "end": v(-8.09, 3.02) * mm});
            skLineSegment(sketch, "E346", {"start": v(-8.09, 3.02) * mm, "end": v(-8.07, 3.13) * mm});
            skLineSegment(sketch, "E347", {"start": v(-8.07, 3.13) * mm, "end": v(-8.05, 3.25) * mm});
            skLineSegment(sketch, "E348", {"start": v(-8.05, 3.25) * mm, "end": v(-8.02, 3.49) * mm});
            skLineSegment(sketch, "E349", {"start": v(-8.02, 3.49) * mm, "end": v(-8, 3.6) * mm});
            skLineSegment(sketch, "E350", {"start": v(-8, 3.6) * mm, "end": v(-8, 3.65) * mm});
            skLineSegment(sketch, "E351", {"start": v(-8, 3.65) * mm, "end": v(-7.98, 3.7) * mm});
            skLineSegment(sketch, "E352", {"start": v(-7.98, 3.7) * mm, "end": v(-7.98, 3.76) * mm});
            skLineSegment(sketch, "E353", {"start": v(-7.98, 3.76) * mm, "end": v(-7.97, 3.8) * mm});
            skLineSegment(sketch, "E354", {"start": v(-7.97, 3.8) * mm, "end": v(-7.96, 3.85) * mm});
            skLineSegment(sketch, "E355", {"start": v(-7.96, 3.85) * mm, "end": v(-7.95, 3.89) * mm});
            skLineSegment(sketch, "E356", {"start": v(-7.95, 3.89) * mm, "end": v(-7.94, 3.93) * mm});
            skLineSegment(sketch, "E357", {"start": v(-7.94, 3.93) * mm, "end": v(-7.94, 3.97) * mm});
            skLineSegment(sketch, "E358", {"start": v(-7.94, 3.97) * mm, "end": v(-7.52, 6.33) * mm});
            skLineSegment(sketch, "E359", {"start": v(-7.52, 6.33) * mm, "end": v(-9.01, 6.56) * mm});
            skLineSegment(sketch, "E360", {"start": v(-9.01, 6.56) * mm, "end": v(-8.93, 7) * mm});
            skLineSegment(sketch, "E361", {"start": v(-8.93, 7) * mm, "end": v(-5.8, 7) * mm});
            skLineSegment(sketch, "E362", {"start": v(-5.8, 7) * mm, "end": v(-8.12, -6.09) * mm});
            skLineSegment(sketch, "E363", {"start": v(-8.12, -6.09) * mm, "end": v(-7.02, -6.33) * mm});
            skLineSegment(sketch, "E364", {"start": v(-7.02, -6.33) * mm, "end": v(-7.1, -6.77) * mm});
            skLineSegment(sketch, "E365", {"start": v(-7.1, -6.77) * mm, "end": v(-9.86, -6.77) * mm});
            skLineSegment(sketch, "E366", {"start": v(-9.86, -6.77) * mm, "end": v(-9.58, -5.26) * mm});
            skLineSegment(sketch, "E367", {"start": v(-9.58, -5.26) * mm, "end": v(-9.78, -5.46) * mm});
            skLineSegment(sketch, "E368", {"start": v(-9.78, -5.46) * mm, "end": v(-9.99, -5.66) * mm});
            skLineSegment(sketch, "E369", {"start": v(-9.99, -5.66) * mm, "end": v(-10.18, -5.84) * mm});
            skLineSegment(sketch, "E370", {"start": v(-10.18, -5.84) * mm, "end": v(-10.38, -6) * mm});
            skLineSegment(sketch, "E371", {"start": v(-10.38, -6) * mm, "end": v(-10.57, -6.16) * mm});
            skLineSegment(sketch, "E372", {"start": v(-10.57, -6.16) * mm, "end": v(-10.77, -6.3) * mm});
            skLineSegment(sketch, "E373", {"start": v(-10.77, -6.3) * mm, "end": v(-10.95, -6.43) * mm});
            skLineSegment(sketch, "E374", {"start": v(-10.95, -6.43) * mm, "end": v(-11.14, -6.54) * mm});
            skLineSegment(sketch, "E375", {"start": v(-11.14, -6.54) * mm, "end": v(-11.33, -6.64) * mm});
            skLineSegment(sketch, "E376", {"start": v(-11.33, -6.64) * mm, "end": v(-11.51, -6.73) * mm});
            skLineSegment(sketch, "E377", {"start": v(-11.51, -6.73) * mm, "end": v(-11.7, -6.8) * mm});
            skLineSegment(sketch, "E378", {"start": v(-11.7, -6.8) * mm, "end": v(-11.87, -6.86) * mm});
            skLineSegment(sketch, "E379", {"start": v(-11.87, -6.86) * mm, "end": v(-12.05, -6.91) * mm});
            skLineSegment(sketch, "E380", {"start": v(-12.05, -6.91) * mm, "end": v(-12.23, -6.94) * mm});
            skLineSegment(sketch, "E381", {"start": v(-12.23, -6.94) * mm, "end": v(-12.4, -6.96) * mm});
            skLineSegment(sketch, "E382", {"start": v(-12.4, -6.96) * mm, "end": v(-12.58, -6.97) * mm});
            skLineSegment(sketch, "E383", {"start": v(-12.58, -6.97) * mm, "end": v(-12.72, -6.97) * mm});
            skLineSegment(sketch, "E384", {"start": v(-12.72, -6.97) * mm, "end": v(-12.86, -6.96) * mm});
            skLineSegment(sketch, "E385", {"start": v(-12.86, -6.96) * mm, "end": v(-13, -6.94) * mm});
            skLineSegment(sketch, "E386", {"start": v(-13, -6.94) * mm, "end": v(-13.13, -6.92) * mm});
            skLineSegment(sketch, "E387", {"start": v(-13.13, -6.92) * mm, "end": v(-13.26, -6.88) * mm});
            skLineSegment(sketch, "E388", {"start": v(-13.26, -6.88) * mm, "end": v(-13.39, -6.85) * mm});
            skLineSegment(sketch, "E389", {"start": v(-13.39, -6.85) * mm, "end": v(-13.51, -6.8) * mm});
            skLineSegment(sketch, "E390", {"start": v(-13.51, -6.8) * mm, "end": v(-13.63, -6.75) * mm});
            skLineSegment(sketch, "E391", {"start": v(-13.63, -6.75) * mm, "end": v(-13.75, -6.69) * mm});
            skLineSegment(sketch, "E392", {"start": v(-13.75, -6.69) * mm, "end": v(-13.86, -6.62) * mm});
            skLineSegment(sketch, "E393", {"start": v(-13.86, -6.62) * mm, "end": v(-13.97, -6.55) * mm});
            skLineSegment(sketch, "E394", {"start": v(-13.97, -6.55) * mm, "end": v(-14.07, -6.48) * mm});
            skLineSegment(sketch, "E395", {"start": v(-14.07, -6.48) * mm, "end": v(-14.17, -6.4) * mm});
            skLineSegment(sketch, "E396", {"start": v(-14.17, -6.4) * mm, "end": v(-14.27, -6.3) * mm});
            skLineSegment(sketch, "E397", {"start": v(-14.27, -6.3) * mm, "end": v(-14.36, -6.2) * mm});
            skLineSegment(sketch, "E398", {"start": v(-14.36, -6.2) * mm, "end": v(-14.45, -6.1) * mm});
            skLineSegment(sketch, "E399", {"start": v(-14.45, -6.1) * mm, "end": v(-14.53, -6) * mm});
            skLineSegment(sketch, "E400", {"start": v(-14.53, -6) * mm, "end": v(-14.6, -5.88) * mm});
            skLineSegment(sketch, "E401", {"start": v(-14.6, -5.88) * mm, "end": v(-14.68, -5.76) * mm});
            skLineSegment(sketch, "E402", {"start": v(-14.68, -5.76) * mm, "end": v(-14.75, -5.64) * mm});
            skLineSegment(sketch, "E403", {"start": v(-14.75, -5.64) * mm, "end": v(-14.81, -5.5) * mm});
            skLineSegment(sketch, "E404", {"start": v(-14.81, -5.5) * mm, "end": v(-14.87, -5.37) * mm});
            skLineSegment(sketch, "E405", {"start": v(-14.87, -5.37) * mm, "end": v(-14.93, -5.22) * mm});
            skLineSegment(sketch, "E406", {"start": v(-14.93, -5.22) * mm, "end": v(-14.98, -5.07) * mm});
            skLineSegment(sketch, "E407", {"start": v(-14.98, -5.07) * mm, "end": v(-15.02, -4.92) * mm});
            skLineSegment(sketch, "E408", {"start": v(-15.02, -4.92) * mm, "end": v(-15.06, -4.76) * mm});
            skLineSegment(sketch, "E409", {"start": v(-15.06, -4.76) * mm, "end": v(-15.1, -4.6) * mm});
            skLineSegment(sketch, "E410", {"start": v(-15.1, -4.6) * mm, "end": v(-15.14, -4.25) * mm});
            skLineSegment(sketch, "E411", {"start": v(-15.14, -4.25) * mm, "end": v(-15.16, -3.89) * mm});
            skLineSegment(sketch, "E412", {"start": v(-15.16, -3.89) * mm, "end": v(-15.16, -3.7) * mm});
            skLineSegment(sketch, "E413", {"start": v(-15.16, -3.7) * mm, "end": v(-15.15, -3.28) * mm});
            skLineSegment(sketch, "E414", {"start": v(-15.15, -3.28) * mm, "end": v(-15.12, -2.88) * mm});
            skLineSegment(sketch, "E415", {"start": v(-15.12, -2.88) * mm, "end": v(-15.06, -2.47) * mm});
            skLineSegment(sketch, "E416", {"start": v(-15.06, -2.47) * mm, "end": v(-14.98, -2.08) * mm});
            skLineSegment(sketch, "E417", {"start": v(-14.98, -2.08) * mm, "end": v(-14.88, -1.69) * mm});
            skLineSegment(sketch, "E418", {"start": v(-14.88, -1.69) * mm, "end": v(-14.76, -1.3) * mm});
            skLineSegment(sketch, "E419", {"start": v(-14.76, -1.3) * mm, "end": v(-14.62, -0.94) * mm});
            skLineSegment(sketch, "E420", {"start": v(-14.62, -0.94) * mm, "end": v(-14.46, -0.59) * mm});
            skLineSegment(sketch, "E421", {"start": v(-14.46, -0.59) * mm, "end": v(-14.28, -0.25) * mm});
            skLineSegment(sketch, "E422", {"start": v(-14.28, -0.25) * mm, "end": v(-14.08, 0.08) * mm});
            skLineSegment(sketch, "E423", {"start": v(-14.08, 0.08) * mm, "end": v(-13.87, 0.39) * mm});
            skLineSegment(sketch, "E424", {"start": v(-13.87, 0.39) * mm, "end": v(-13.64, 0.68) * mm});
            skLineSegment(sketch, "E425", {"start": v(-13.64, 0.68) * mm, "end": v(-13.4, 0.96) * mm});
            skLineSegment(sketch, "E426", {"start": v(-13.4, 0.96) * mm, "end": v(-13.13, 1.22) * mm});
            skLineSegment(sketch, "E427", {"start": v(-13.13, 1.22) * mm, "end": v(-12.85, 1.46) * mm});
            skLineSegment(sketch, "E428", {"start": v(-12.85, 1.46) * mm, "end": v(-12.56, 1.68) * mm});
            skLineSegment(sketch, "E429", {"start": v(-12.56, 1.68) * mm, "end": v(-12.25, 1.88) * mm});
            skLineSegment(sketch, "E430", {"start": v(-12.25, 1.88) * mm, "end": v(-11.93, 2.06) * mm});
            skLineSegment(sketch, "E431", {"start": v(-11.93, 2.06) * mm, "end": v(-11.6, 2.21) * mm});
            skLineSegment(sketch, "E432", {"start": v(-11.6, 2.21) * mm, "end": v(-11.26, 2.34) * mm});
            skLineSegment(sketch, "E433", {"start": v(-11.26, 2.34) * mm, "end": v(-10.9, 2.44) * mm});
            skLineSegment(sketch, "E434", {"start": v(-10.9, 2.44) * mm, "end": v(-10.53, 2.51) * mm});
            skLineSegment(sketch, "E435", {"start": v(-10.53, 2.51) * mm, "end": v(-10.16, 2.56) * mm});
            skLineSegment(sketch, "E436", {"start": v(-10.16, 2.56) * mm, "end": v(-9.78, 2.57) * mm});
            skLineSegment(sketch, "E437", {"start": v(-9.78, 2.57) * mm, "end": v(-9.54, 2.57) * mm});
            skLineSegment(sketch, "E438", {"start": v(-9.54, 2.57) * mm, "end": v(-9.32, 2.56) * mm});
            skLineSegment(sketch, "E439", {"start": v(-9.32, 2.56) * mm, "end": v(-9.1, 2.54) * mm});
            skLineSegment(sketch, "E440", {"start": v(-9.1, 2.54) * mm, "end": v(-8.9, 2.51) * mm});
            skLineSegment(sketch, "E441", {"start": v(-8.9, 2.51) * mm, "end": v(-8.7, 2.48) * mm});
            skLineSegment(sketch, "E442", {"start": v(-8.7, 2.48) * mm, "end": v(-8.52, 2.44) * mm});
            skLineSegment(sketch, "E443", {"start": v(-8.52, 2.44) * mm, "end": v(-8.35, 2.4) * mm});
            skLineSegment(sketch, "E444", {"start": v(-8.35, 2.4) * mm, "end": v(-8.18, 2.35) * mm});
            skLineSegment(sketch, "E445", {"start": v(-8.4, 1.34) * mm, "end": v(-8.57, 1.45) * mm});
            skLineSegment(sketch, "E446", {"start": v(-8.57, 1.45) * mm, "end": v(-8.74, 1.54) * mm});
            skLineSegment(sketch, "E447", {"start": v(-8.74, 1.54) * mm, "end": v(-8.92, 1.62) * mm});
            skLineSegment(sketch, "E448", {"start": v(-8.92, 1.62) * mm, "end": v(-9.1, 1.7) * mm});
            skLineSegment(sketch, "E449", {"start": v(-9.1, 1.7) * mm, "end": v(-9.2, 1.72) * mm});
            skLineSegment(sketch, "E450", {"start": v(-9.2, 1.72) * mm, "end": v(-9.29, 1.75) * mm});
            skLineSegment(sketch, "E451", {"start": v(-9.29, 1.75) * mm, "end": v(-9.39, 1.77) * mm});
            skLineSegment(sketch, "E452", {"start": v(-9.39, 1.77) * mm, "end": v(-9.5, 1.79) * mm});
            skLineSegment(sketch, "E453", {"start": v(-9.5, 1.79) * mm, "end": v(-9.6, 1.8) * mm});
            skLineSegment(sketch, "E454", {"start": v(-9.6, 1.8) * mm, "end": v(-9.72, 1.8) * mm});
            skLineSegment(sketch, "E455", {"start": v(-9.72, 1.8) * mm, "end": v(-9.84, 1.81) * mm});
            skLineSegment(sketch, "E456", {"start": v(-9.84, 1.81) * mm, "end": v(-9.97, 1.82) * mm});
            skLineSegment(sketch, "E457", {"start": v(-9.97, 1.82) * mm, "end": v(-10.1, 1.81) * mm});
            skLineSegment(sketch, "E458", {"start": v(-10.1, 1.81) * mm, "end": v(-10.23, 1.8) * mm});
            skLineSegment(sketch, "E459", {"start": v(-10.23, 1.8) * mm, "end": v(-10.35, 1.79) * mm});
            skLineSegment(sketch, "E460", {"start": v(-10.35, 1.79) * mm, "end": v(-10.48, 1.76) * mm});
            skLineSegment(sketch, "E461", {"start": v(-10.48, 1.76) * mm, "end": v(-10.6, 1.73) * mm});
            skLineSegment(sketch, "E462", {"start": v(-10.6, 1.73) * mm, "end": v(-10.72, 1.7) * mm});
            skLineSegment(sketch, "E463", {"start": v(-10.72, 1.7) * mm, "end": v(-10.83, 1.65) * mm});
            skLineSegment(sketch, "E464", {"start": v(-10.83, 1.65) * mm, "end": v(-10.95, 1.6) * mm});
            skLineSegment(sketch, "E465", {"start": v(-10.95, 1.6) * mm, "end": v(-11.06, 1.54) * mm});
            skLineSegment(sketch, "E466", {"start": v(-11.06, 1.54) * mm, "end": v(-11.28, 1.4) * mm});
            skLineSegment(sketch, "E467", {"start": v(-11.28, 1.4) * mm, "end": v(-11.5, 1.25) * mm});
            skLineSegment(sketch, "E468", {"start": v(-11.5, 1.25) * mm, "end": v(-11.7, 1.08) * mm});
            skLineSegment(sketch, "E469", {"start": v(-11.7, 1.08) * mm, "end": v(-11.8, 0.98) * mm});
            skLineSegment(sketch, "E470", {"start": v(-11.8, 0.98) * mm, "end": v(-11.98, 0.79) * mm});
            skLineSegment(sketch, "E471", {"start": v(-11.98, 0.79) * mm, "end": v(-12.16, 0.57) * mm});
            skLineSegment(sketch, "E472", {"start": v(-12.16, 0.57) * mm, "end": v(-12.33, 0.34) * mm});
            skLineSegment(sketch, "E473", {"start": v(-12.33, 0.34) * mm, "end": v(-12.49, 0.1) * mm});
            skLineSegment(sketch, "E474", {"start": v(-12.49, 0.1) * mm, "end": v(-12.63, -0.17) * mm});
            skLineSegment(sketch, "E475", {"start": v(-12.63, -0.17) * mm, "end": v(-12.77, -0.44) * mm});
            skLineSegment(sketch, "E476", {"start": v(-12.77, -0.44) * mm, "end": v(-12.9, -0.72) * mm});
            skLineSegment(sketch, "E477", {"start": v(-12.9, -0.72) * mm, "end": v(-13, -1.01) * mm});
            skLineSegment(sketch, "E478", {"start": v(-13, -1.01) * mm, "end": v(-13.1, -1.31) * mm});
            skLineSegment(sketch, "E479", {"start": v(-13.1, -1.31) * mm, "end": v(-13.27, -1.92) * mm});
            skLineSegment(sketch, "E480", {"start": v(-13.27, -1.92) * mm, "end": v(-13.33, -2.23) * mm});
            skLineSegment(sketch, "E481", {"start": v(-13.33, -2.23) * mm, "end": v(-13.38, -2.55) * mm});
            skLineSegment(sketch, "E482", {"start": v(-13.38, -2.55) * mm, "end": v(-13.43, -3.17) * mm});
            skLineSegment(sketch, "E483", {"start": v(-13.43, -3.17) * mm, "end": v(-13.44, -3.48) * mm});
            skLineSegment(sketch, "E484", {"start": v(-13.44, -3.48) * mm, "end": v(-13.44, -3.63) * mm});
            skLineSegment(sketch, "E485", {"start": v(-13.44, -3.63) * mm, "end": v(-13.43, -3.78) * mm});
            skLineSegment(sketch, "E486", {"start": v(-13.43, -3.78) * mm, "end": v(-13.42, -3.92) * mm});
            skLineSegment(sketch, "E487", {"start": v(-13.42, -3.92) * mm, "end": v(-13.4, -4.05) * mm});
            skLineSegment(sketch, "E488", {"start": v(-13.4, -4.05) * mm, "end": v(-13.39, -4.18) * mm});
            skLineSegment(sketch, "E489", {"start": v(-13.39, -4.18) * mm, "end": v(-13.36, -4.3) * mm});
            skLineSegment(sketch, "E490", {"start": v(-13.36, -4.3) * mm, "end": v(-13.33, -4.42) * mm});
            skLineSegment(sketch, "E491", {"start": v(-13.33, -4.42) * mm, "end": v(-13.3, -4.53) * mm});
            skLineSegment(sketch, "E492", {"start": v(-13.3, -4.53) * mm, "end": v(-13.27, -4.63) * mm});
            skLineSegment(sketch, "E493", {"start": v(-13.27, -4.63) * mm, "end": v(-13.23, -4.73) * mm});
            skLineSegment(sketch, "E494", {"start": v(-13.23, -4.73) * mm, "end": v(-13.2, -4.83) * mm});
            skLineSegment(sketch, "E495", {"start": v(-13.2, -4.83) * mm, "end": v(-13.15, -4.92) * mm});
            skLineSegment(sketch, "E496", {"start": v(-13.15, -4.92) * mm, "end": v(-13.1, -5) * mm});
            skLineSegment(sketch, "E497", {"start": v(-13.1, -5) * mm, "end": v(-13.06, -5.09) * mm});
            skLineSegment(sketch, "E498", {"start": v(-13.06, -5.09) * mm, "end": v(-13, -5.16) * mm});
            skLineSegment(sketch, "E499", {"start": v(-13, -5.16) * mm, "end": v(-12.95, -5.24) * mm});
            skLineSegment(sketch, "E500", {"start": v(-12.95, -5.24) * mm, "end": v(-12.9, -5.3) * mm});
            skLineSegment(sketch, "E501", {"start": v(-12.9, -5.3) * mm, "end": v(-12.84, -5.36) * mm});
            skLineSegment(sketch, "E502", {"start": v(-12.84, -5.36) * mm, "end": v(-12.78, -5.42) * mm});
            skLineSegment(sketch, "E503", {"start": v(-12.78, -5.42) * mm, "end": v(-12.72, -5.47) * mm});
            skLineSegment(sketch, "E504", {"start": v(-12.72, -5.47) * mm, "end": v(-12.65, -5.52) * mm});
            skLineSegment(sketch, "E505", {"start": v(-12.65, -5.52) * mm, "end": v(-12.59, -5.56) * mm});
            skLineSegment(sketch, "E506", {"start": v(-12.59, -5.56) * mm, "end": v(-12.52, -5.6) * mm});
            skLineSegment(sketch, "E507", {"start": v(-12.52, -5.6) * mm, "end": v(-12.45, -5.63) * mm});
            skLineSegment(sketch, "E508", {"start": v(-12.45, -5.63) * mm, "end": v(-12.38, -5.66) * mm});
            skLineSegment(sketch, "E509", {"start": v(-12.38, -5.66) * mm, "end": v(-12.3, -5.69) * mm});
            skLineSegment(sketch, "E510", {"start": v(-12.3, -5.69) * mm, "end": v(-12.23, -5.71) * mm});
            skLineSegment(sketch, "E511", {"start": v(-12.23, -5.71) * mm, "end": v(-12.16, -5.73) * mm});
            skLineSegment(sketch, "E512", {"start": v(-12.16, -5.73) * mm, "end": v(-12.08, -5.74) * mm});
            skLineSegment(sketch, "E513", {"start": v(-12.08, -5.74) * mm, "end": v(-12, -5.75) * mm});
            skLineSegment(sketch, "E514", {"start": v(-12, -5.75) * mm, "end": v(-11.93, -5.76) * mm});
            skLineSegment(sketch, "E515", {"start": v(-11.93, -5.76) * mm, "end": v(-11.86, -5.76) * mm});
            skLineSegment(sketch, "E516", {"start": v(-11.86, -5.76) * mm, "end": v(-11.72, -5.75) * mm});
            skLineSegment(sketch, "E517", {"start": v(-11.72, -5.75) * mm, "end": v(-11.58, -5.74) * mm});
            skLineSegment(sketch, "E518", {"start": v(-11.58, -5.74) * mm, "end": v(-11.44, -5.71) * mm});
            skLineSegment(sketch, "E519", {"start": v(-11.44, -5.71) * mm, "end": v(-11.3, -5.67) * mm});
            skLineSegment(sketch, "E520", {"start": v(-11.3, -5.67) * mm, "end": v(-11.15, -5.62) * mm});
            skLineSegment(sketch, "E521", {"start": v(-11.15, -5.62) * mm, "end": v(-11, -5.56) * mm});
            skLineSegment(sketch, "E522", {"start": v(-11, -5.56) * mm, "end": v(-10.84, -5.5) * mm});
            skLineSegment(sketch, "E523", {"start": v(-10.84, -5.5) * mm, "end": v(-10.69, -5.41) * mm});
            skLineSegment(sketch, "E524", {"start": v(-10.69, -5.41) * mm, "end": v(-10.53, -5.32) * mm});
            skLineSegment(sketch, "E525", {"start": v(-10.53, -5.32) * mm, "end": v(-10.37, -5.21) * mm});
            skLineSegment(sketch, "E526", {"start": v(-10.37, -5.21) * mm, "end": v(-10.21, -5.1) * mm});
            skLineSegment(sketch, "E527", {"start": v(-10.21, -5.1) * mm, "end": v(-10.06, -4.98) * mm});
            skLineSegment(sketch, "E528", {"start": v(-10.06, -4.98) * mm, "end": v(-9.9, -4.85) * mm});
            skLineSegment(sketch, "E529", {"start": v(-9.9, -4.85) * mm, "end": v(-9.6, -4.57) * mm});
            skLineSegment(sketch, "E530", {"start": v(-9.6, -4.57) * mm, "end": v(-9.46, -4.41) * mm});
            skLineSegment(sketch, "E531", {"start": v(-9.46, -4.41) * mm, "end": v(-8.4, 1.34) * mm});
            skLineSegment(sketch, "E532", {"start": v(3.57, 0.46) * mm, "end": v(3.73, 0.68) * mm});
            skLineSegment(sketch, "E533", {"start": v(3.73, 0.68) * mm, "end": v(4.08, 1.1) * mm});
            skLineSegment(sketch, "E534", {"start": v(4.08, 1.1) * mm, "end": v(4.26, 1.3) * mm});
            skLineSegment(sketch, "E535", {"start": v(4.26, 1.3) * mm, "end": v(4.45, 1.5) * mm});
            skLineSegment(sketch, "E536", {"start": v(4.45, 1.5) * mm, "end": v(4.65, 1.66) * mm});
            skLineSegment(sketch, "E537", {"start": v(4.65, 1.66) * mm, "end": v(4.84, 1.82) * mm});
            skLineSegment(sketch, "E538", {"start": v(4.84, 1.82) * mm, "end": v(5.04, 1.97) * mm});
            skLineSegment(sketch, "E539", {"start": v(5.04, 1.97) * mm, "end": v(5.24, 2.1) * mm});
            skLineSegment(sketch, "E540", {"start": v(5.24, 2.1) * mm, "end": v(5.44, 2.23) * mm});
            skLineSegment(sketch, "E541", {"start": v(5.44, 2.23) * mm, "end": v(5.64, 2.33) * mm});
            skLineSegment(sketch, "E542", {"start": v(5.64, 2.33) * mm, "end": v(5.84, 2.42) * mm});
            skLineSegment(sketch, "E543", {"start": v(5.84, 2.42) * mm, "end": v(5.95, 2.46) * mm});
            skLineSegment(sketch, "E544", {"start": v(5.95, 2.46) * mm, "end": v(6.05, 2.49) * mm});
            skLineSegment(sketch, "E545", {"start": v(6.05, 2.49) * mm, "end": v(6.15, 2.52) * mm});
            skLineSegment(sketch, "E546", {"start": v(6.15, 2.52) * mm, "end": v(6.25, 2.54) * mm});
            skLineSegment(sketch, "E547", {"start": v(6.25, 2.54) * mm, "end": v(6.36, 2.56) * mm});
            skLineSegment(sketch, "E548", {"start": v(6.36, 2.56) * mm, "end": v(6.46, 2.57) * mm});
            skLineSegment(sketch, "E549", {"start": v(6.46, 2.57) * mm, "end": v(6.56, 2.58) * mm});
            skLineSegment(sketch, "E550", {"start": v(6.56, 2.58) * mm, "end": v(6.66, 2.58) * mm});
            skLineSegment(sketch, "E551", {"start": v(6.66, 2.58) * mm, "end": v(6.76, 2.58) * mm});
            skLineSegment(sketch, "E552", {"start": v(6.76, 2.58) * mm, "end": v(6.85, 2.57) * mm});
            skLineSegment(sketch, "E553", {"start": v(6.85, 2.57) * mm, "end": v(6.95, 2.56) * mm});
            skLineSegment(sketch, "E554", {"start": v(6.95, 2.56) * mm, "end": v(7.04, 2.55) * mm});
            skLineSegment(sketch, "E555", {"start": v(7.04, 2.55) * mm, "end": v(7.13, 2.53) * mm});
            skLineSegment(sketch, "E556", {"start": v(7.13, 2.53) * mm, "end": v(7.22, 2.5) * mm});
            skLineSegment(sketch, "E557", {"start": v(7.22, 2.5) * mm, "end": v(7.3, 2.48) * mm});
            skLineSegment(sketch, "E558", {"start": v(7.3, 2.48) * mm, "end": v(7.38, 2.45) * mm});
            skLineSegment(sketch, "E559", {"start": v(7.38, 2.45) * mm, "end": v(7.46, 2.42) * mm});
            skLineSegment(sketch, "E560", {"start": v(7.46, 2.42) * mm, "end": v(7.54, 2.38) * mm});
            skLineSegment(sketch, "E561", {"start": v(7.54, 2.38) * mm, "end": v(7.61, 2.33) * mm});
            skLineSegment(sketch, "E562", {"start": v(7.61, 2.33) * mm, "end": v(7.68, 2.29) * mm});
            skLineSegment(sketch, "E563", {"start": v(7.68, 2.29) * mm, "end": v(7.75, 2.24) * mm});
            skLineSegment(sketch, "E564", {"start": v(7.75, 2.24) * mm, "end": v(7.81, 2.18) * mm});
            skLineSegment(sketch, "E565", {"start": v(7.81, 2.18) * mm, "end": v(7.88, 2.12) * mm});
            skLineSegment(sketch, "E566", {"start": v(7.88, 2.12) * mm, "end": v(7.93, 2.06) * mm});
            skLineSegment(sketch, "E567", {"start": v(7.93, 2.06) * mm, "end": v(8, 2) * mm});
            skLineSegment(sketch, "E568", {"start": v(8, 2) * mm, "end": v(8.05, 1.92) * mm});
            skLineSegment(sketch, "E569", {"start": v(8.05, 1.92) * mm, "end": v(8.1, 1.85) * mm});
            skLineSegment(sketch, "E570", {"start": v(8.1, 1.85) * mm, "end": v(8.14, 1.77) * mm});
            skLineSegment(sketch, "E571", {"start": v(8.14, 1.77) * mm, "end": v(8.19, 1.7) * mm});
            skLineSegment(sketch, "E572", {"start": v(8.19, 1.7) * mm, "end": v(8.22, 1.6) * mm});
            skLineSegment(sketch, "E573", {"start": v(8.22, 1.6) * mm, "end": v(8.26, 1.52) * mm});
            skLineSegment(sketch, "E574", {"start": v(8.26, 1.52) * mm, "end": v(8.3, 1.43) * mm});
            skLineSegment(sketch, "E575", {"start": v(8.3, 1.43) * mm, "end": v(8.32, 1.33) * mm});
            skLineSegment(sketch, "E576", {"start": v(8.32, 1.33) * mm, "end": v(8.34, 1.24) * mm});
            skLineSegment(sketch, "E577", {"start": v(8.34, 1.24) * mm, "end": v(8.36, 1.13) * mm});
            skLineSegment(sketch, "E578", {"start": v(8.36, 1.13) * mm, "end": v(8.38, 1.03) * mm});
            skLineSegment(sketch, "E579", {"start": v(8.38, 1.03) * mm, "end": v(8.4, 0.92) * mm});
            skLineSegment(sketch, "E580", {"start": v(8.4, 0.92) * mm, "end": v(8.4, 0.8) * mm});
            skLineSegment(sketch, "E581", {"start": v(8.4, 0.8) * mm, "end": v(8.4, 0.69) * mm});
            skLineSegment(sketch, "E582", {"start": v(8.4, 0.69) * mm, "end": v(8.4, 0.57) * mm});
            skLineSegment(sketch, "E583", {"start": v(8.4, 0.57) * mm, "end": v(8.4, 0.53) * mm});
            skLineSegment(sketch, "E584", {"start": v(8.4, 0.53) * mm, "end": v(8.4, 0.5) * mm});
            skLineSegment(sketch, "E585", {"start": v(8.4, 0.5) * mm, "end": v(8.4, 0.45) * mm});
            skLineSegment(sketch, "E586", {"start": v(8.4, 0.45) * mm, "end": v(8.4, 0.4) * mm});
            skLineSegment(sketch, "E587", {"start": v(8.4, 0.4) * mm, "end": v(8.4, 0.32) * mm});
            skLineSegment(sketch, "E588", {"start": v(8.4, 0.32) * mm, "end": v(8.4, 0.22) * mm});
            skLineSegment(sketch, "E589", {"start": v(8.4, 0.22) * mm, "end": v(8.38, 0.11) * mm});
            skLineSegment(sketch, "E590", {"start": v(8.38, 0.11) * mm, "end": v(8.35, -0.1) * mm});
            skLineSegment(sketch, "E591", {"start": v(8.35, -0.1) * mm, "end": v(8.33, -0.22) * mm});
            skLineSegment(sketch, "E592", {"start": v(8.33, -0.22) * mm, "end": v(8.32, -0.33) * mm});
            skLineSegment(sketch, "E593", {"start": v(8.32, -0.33) * mm, "end": v(8.28, -0.57) * mm});
            skLineSegment(sketch, "E594", {"start": v(8.28, -0.57) * mm, "end": v(8.26, -0.7) * mm});
            skLineSegment(sketch, "E595", {"start": v(8.26, -0.7) * mm, "end": v(8.24, -0.81) * mm});
            skLineSegment(sketch, "E596", {"start": v(8.24, -0.81) * mm, "end": v(8.2, -1.04) * mm});
            skLineSegment(sketch, "E597", {"start": v(8.2, -1.04) * mm, "end": v(8.19, -1.15) * mm});
            skLineSegment(sketch, "E598", {"start": v(8.19, -1.15) * mm, "end": v(7.33, -6.09) * mm});
            skLineSegment(sketch, "E599", {"start": v(7.33, -6.09) * mm, "end": v(8.6, -6.33) * mm});
            skLineSegment(sketch, "E600", {"start": v(8.6, -6.33) * mm, "end": v(8.52, -6.77) * mm});
            skLineSegment(sketch, "E601", {"start": v(8.52, -6.77) * mm, "end": v(5.6, -6.77) * mm});
            skLineSegment(sketch, "E602", {"start": v(5.6, -6.77) * mm, "end": v(6.6, -1.13) * mm});
            skLineSegment(sketch, "E603", {"start": v(6.6, -1.13) * mm, "end": v(6.62, -1.03) * mm});
            skLineSegment(sketch, "E604", {"start": v(6.62, -1.03) * mm, "end": v(6.66, -0.8) * mm});
            skLineSegment(sketch, "E605", {"start": v(6.66, -0.8) * mm, "end": v(6.68, -0.7) * mm});
            skLineSegment(sketch, "E606", {"start": v(6.68, -0.7) * mm, "end": v(6.7, -0.57) * mm});
            skLineSegment(sketch, "E607", {"start": v(6.7, -0.57) * mm, "end": v(6.73, -0.34) * mm});
            skLineSegment(sketch, "E608", {"start": v(6.73, -0.34) * mm, "end": v(6.74, -0.23) * mm});
            skLineSegment(sketch, "E609", {"start": v(6.74, -0.23) * mm, "end": v(6.76, -0.12) * mm});
            skLineSegment(sketch, "E610", {"start": v(6.76, -0.12) * mm, "end": v(6.78, -0.01) * mm});
            skLineSegment(sketch, "E611", {"start": v(6.78, -0.01) * mm, "end": v(6.8, 0.08) * mm});
            skLineSegment(sketch, "E612", {"start": v(6.8, 0.08) * mm, "end": v(6.8, 0.18) * mm});
            skLineSegment(sketch, "E613", {"start": v(6.8, 0.18) * mm, "end": v(6.8, 0.22) * mm});
            skLineSegment(sketch, "E614", {"start": v(6.8, 0.22) * mm, "end": v(6.8, 0.27) * mm});
            skLineSegment(sketch, "E615", {"start": v(6.8, 0.27) * mm, "end": v(6.81, 0.3) * mm});
            skLineSegment(sketch, "E616", {"start": v(6.81, 0.3) * mm, "end": v(6.82, 0.35) * mm});
            skLineSegment(sketch, "E617", {"start": v(6.82, 0.35) * mm, "end": v(6.82, 0.38) * mm});
            skLineSegment(sketch, "E618", {"start": v(6.82, 0.38) * mm, "end": v(6.82, 0.42) * mm});
            skLineSegment(sketch, "E619", {"start": v(6.82, 0.42) * mm, "end": v(6.82, 0.45) * mm});
            skLineSegment(sketch, "E620", {"start": v(6.82, 0.45) * mm, "end": v(6.82, 0.48) * mm});
            skLineSegment(sketch, "E621", {"start": v(6.82, 0.48) * mm, "end": v(6.82, 0.59) * mm});
            skLineSegment(sketch, "E622", {"start": v(6.82, 0.59) * mm, "end": v(6.8, 0.69) * mm});
            skLineSegment(sketch, "E623", {"start": v(6.8, 0.69) * mm, "end": v(6.8, 0.78) * mm});
            skLineSegment(sketch, "E624", {"start": v(6.8, 0.78) * mm, "end": v(6.78, 0.83) * mm});
            skLineSegment(sketch, "E625", {"start": v(6.78, 0.83) * mm, "end": v(6.77, 0.87) * mm});
            skLineSegment(sketch, "E626", {"start": v(6.77, 0.87) * mm, "end": v(6.76, 0.91) * mm});
            skLineSegment(sketch, "E627", {"start": v(6.76, 0.91) * mm, "end": v(6.74, 0.96) * mm});
            skLineSegment(sketch, "E628", {"start": v(6.74, 0.96) * mm, "end": v(6.72, 1) * mm});
            skLineSegment(sketch, "E629", {"start": v(6.72, 1) * mm, "end": v(6.7, 1.04) * mm});
            skLineSegment(sketch, "E630", {"start": v(6.7, 1.04) * mm, "end": v(6.69, 1.07) * mm});
            skLineSegment(sketch, "E631", {"start": v(6.69, 1.07) * mm, "end": v(6.66, 1.1) * mm});
            skLineSegment(sketch, "E632", {"start": v(6.66, 1.1) * mm, "end": v(6.64, 1.14) * mm});
            skLineSegment(sketch, "E633", {"start": v(6.64, 1.14) * mm, "end": v(6.62, 1.18) * mm});
            skLineSegment(sketch, "E634", {"start": v(6.62, 1.18) * mm, "end": v(6.6, 1.21) * mm});
            skLineSegment(sketch, "E635", {"start": v(6.6, 1.21) * mm, "end": v(6.56, 1.24) * mm});
            skLineSegment(sketch, "E636", {"start": v(6.56, 1.24) * mm, "end": v(6.53, 1.27) * mm});
            skLineSegment(sketch, "E637", {"start": v(6.53, 1.27) * mm, "end": v(6.5, 1.3) * mm});
            skLineSegment(sketch, "E638", {"start": v(6.5, 1.3) * mm, "end": v(6.47, 1.32) * mm});
            skLineSegment(sketch, "E639", {"start": v(6.47, 1.32) * mm, "end": v(6.43, 1.34) * mm});
            skLineSegment(sketch, "E640", {"start": v(6.43, 1.34) * mm, "end": v(6.4, 1.36) * mm});
            skLineSegment(sketch, "E641", {"start": v(6.4, 1.36) * mm, "end": v(6.36, 1.38) * mm});
            skLineSegment(sketch, "E642", {"start": v(6.36, 1.38) * mm, "end": v(6.31, 1.4) * mm});
            skLineSegment(sketch, "E643", {"start": v(6.31, 1.4) * mm, "end": v(6.27, 1.41) * mm});
            skLineSegment(sketch, "E644", {"start": v(6.27, 1.41) * mm, "end": v(6.23, 1.42) * mm});
            skLineSegment(sketch, "E645", {"start": v(6.23, 1.42) * mm, "end": v(6.18, 1.43) * mm});
            skLineSegment(sketch, "E646", {"start": v(6.18, 1.43) * mm, "end": v(6.13, 1.44) * mm});
            skLineSegment(sketch, "E647", {"start": v(6.13, 1.44) * mm, "end": v(6.08, 1.44) * mm});
            skLineSegment(sketch, "E648", {"start": v(6.08, 1.44) * mm, "end": v(6.03, 1.45) * mm});
            skLineSegment(sketch, "E649", {"start": v(6.03, 1.45) * mm, "end": v(5.98, 1.45) * mm});
            skLineSegment(sketch, "E650", {"start": v(5.98, 1.45) * mm, "end": v(5.92, 1.45) * mm});
            skLineSegment(sketch, "E651", {"start": v(5.92, 1.45) * mm, "end": v(5.86, 1.44) * mm});
            skLineSegment(sketch, "E652", {"start": v(5.86, 1.44) * mm, "end": v(5.8, 1.43) * mm});
            skLineSegment(sketch, "E653", {"start": v(5.8, 1.43) * mm, "end": v(5.74, 1.42) * mm});
            skLineSegment(sketch, "E654", {"start": v(5.74, 1.42) * mm, "end": v(5.68, 1.4) * mm});
            skLineSegment(sketch, "E655", {"start": v(5.68, 1.4) * mm, "end": v(5.62, 1.38) * mm});
            skLineSegment(sketch, "E656", {"start": v(5.62, 1.38) * mm, "end": v(5.55, 1.36) * mm});
            skLineSegment(sketch, "E657", {"start": v(5.55, 1.36) * mm, "end": v(5.48, 1.33) * mm});
            skLineSegment(sketch, "E658", {"start": v(5.48, 1.33) * mm, "end": v(5.35, 1.27) * mm});
            skLineSegment(sketch, "E659", {"start": v(5.35, 1.27) * mm, "end": v(5.21, 1.2) * mm});
            skLineSegment(sketch, "E660", {"start": v(5.21, 1.2) * mm, "end": v(5.07, 1.1) * mm});
            skLineSegment(sketch, "E661", {"start": v(5.07, 1.1) * mm, "end": v(4.93, 1.01) * mm});
            skLineSegment(sketch, "E662", {"start": v(4.93, 1.01) * mm, "end": v(4.8, 0.91) * mm});
            skLineSegment(sketch, "E663", {"start": v(4.8, 0.91) * mm, "end": v(4.65, 0.8) * mm});
            skLineSegment(sketch, "E664", {"start": v(4.65, 0.8) * mm, "end": v(4.52, 0.68) * mm});
            skLineSegment(sketch, "E665", {"start": v(4.52, 0.68) * mm, "end": v(4.38, 0.56) * mm});
            skLineSegment(sketch, "E666", {"start": v(4.38, 0.56) * mm, "end": v(4.25, 0.42) * mm});
            skLineSegment(sketch, "E667", {"start": v(4.25, 0.42) * mm, "end": v(4, 0.15) * mm});
            skLineSegment(sketch, "E668", {"start": v(4, 0.15) * mm, "end": v(3.9, 0) * mm});
            skLineSegment(sketch, "E669", {"start": v(3.9, 0) * mm, "end": v(3.79, -0.14) * mm});
            skLineSegment(sketch, "E670", {"start": v(3.79, -0.14) * mm, "end": v(3.69, -0.3) * mm});
            skLineSegment(sketch, "E671", {"start": v(3.69, -0.3) * mm, "end": v(3.6, -0.44) * mm});
            skLineSegment(sketch, "E672", {"start": v(3.6, -0.44) * mm, "end": v(3.52, -0.6) * mm});
            skLineSegment(sketch, "E673", {"start": v(3.52, -0.6) * mm, "end": v(3.45, -0.75) * mm});
            skLineSegment(sketch, "E674", {"start": v(3.45, -0.75) * mm, "end": v(3.39, -0.9) * mm});
            skLineSegment(sketch, "E675", {"start": v(3.39, -0.9) * mm, "end": v(3.36, -0.97) * mm});
            skLineSegment(sketch, "E676", {"start": v(3.36, -0.97) * mm, "end": v(3.34, -1.04) * mm});
            skLineSegment(sketch, "E677", {"start": v(3.34, -1.04) * mm, "end": v(3.33, -1.12) * mm});
            skLineSegment(sketch, "E678", {"start": v(3.33, -1.12) * mm, "end": v(3.31, -1.19) * mm});
            skLineSegment(sketch, "E679", {"start": v(3.31, -1.19) * mm, "end": v(2.35, -6.77) * mm});
            skLineSegment(sketch, "E680", {"start": v(2.35, -6.77) * mm, "end": v(0.75, -6.77) * mm});
            skLineSegment(sketch, "E681", {"start": v(0.75, -6.77) * mm, "end": v(1.73, -1.13) * mm});
            skLineSegment(sketch, "E682", {"start": v(1.73, -1.13) * mm, "end": v(1.75, -1.03) * mm});
            skLineSegment(sketch, "E683", {"start": v(1.75, -1.03) * mm, "end": v(1.8, -0.8) * mm});
            skLineSegment(sketch, "E684", {"start": v(1.8, -0.8) * mm, "end": v(1.81, -0.7) * mm});
            skLineSegment(sketch, "E685", {"start": v(1.81, -0.7) * mm, "end": v(1.83, -0.57) * mm});
            skLineSegment(sketch, "E686", {"start": v(1.83, -0.57) * mm, "end": v(1.87, -0.34) * mm});
            skLineSegment(sketch, "E687", {"start": v(1.87, -0.34) * mm, "end": v(1.89, -0.23) * mm});
            skLineSegment(sketch, "E688", {"start": v(1.89, -0.23) * mm, "end": v(1.9, -0.12) * mm});
            skLineSegment(sketch, "E689", {"start": v(1.9, -0.12) * mm, "end": v(1.92, -0.01) * mm});
            skLineSegment(sketch, "E690", {"start": v(1.92, -0.01) * mm, "end": v(1.94, 0.08) * mm});
            skLineSegment(sketch, "E691", {"start": v(1.94, 0.08) * mm, "end": v(1.95, 0.18) * mm});
            skLineSegment(sketch, "E692", {"start": v(1.95, 0.18) * mm, "end": v(1.95, 0.22) * mm});
            skLineSegment(sketch, "E693", {"start": v(1.95, 0.22) * mm, "end": v(1.96, 0.27) * mm});
            skLineSegment(sketch, "E694", {"start": v(1.96, 0.27) * mm, "end": v(1.97, 0.3) * mm});
            skLineSegment(sketch, "E695", {"start": v(1.97, 0.3) * mm, "end": v(1.97, 0.35) * mm});
            skLineSegment(sketch, "E696", {"start": v(1.97, 0.35) * mm, "end": v(1.97, 0.38) * mm});
            skLineSegment(sketch, "E697", {"start": v(1.97, 0.38) * mm, "end": v(1.97, 0.42) * mm});
            skLineSegment(sketch, "E698", {"start": v(1.97, 0.42) * mm, "end": v(1.98, 0.45) * mm});
            skLineSegment(sketch, "E699", {"start": v(1.98, 0.45) * mm, "end": v(1.98, 0.48) * mm});
            skLineSegment(sketch, "E700", {"start": v(1.98, 0.48) * mm, "end": v(1.97, 0.59) * mm});
            skLineSegment(sketch, "E701", {"start": v(1.97, 0.59) * mm, "end": v(1.96, 0.69) * mm});
            skLineSegment(sketch, "E702", {"start": v(1.96, 0.69) * mm, "end": v(1.96, 0.74) * mm});
            skLineSegment(sketch, "E703", {"start": v(1.96, 0.74) * mm, "end": v(1.95, 0.78) * mm});
            skLineSegment(sketch, "E704", {"start": v(1.95, 0.78) * mm, "end": v(1.94, 0.83) * mm});
            skLineSegment(sketch, "E705", {"start": v(1.94, 0.83) * mm, "end": v(1.92, 0.87) * mm});
            skLineSegment(sketch, "E706", {"start": v(1.92, 0.87) * mm, "end": v(1.9, 0.91) * mm});
            skLineSegment(sketch, "E707", {"start": v(1.9, 0.91) * mm, "end": v(1.9, 0.96) * mm});
            skLineSegment(sketch, "E708", {"start": v(1.9, 0.96) * mm, "end": v(1.88, 1) * mm});
            skLineSegment(sketch, "E709", {"start": v(1.88, 1) * mm, "end": v(1.86, 1.04) * mm});
            skLineSegment(sketch, "E710", {"start": v(1.86, 1.04) * mm, "end": v(1.84, 1.07) * mm});
            skLineSegment(sketch, "E711", {"start": v(1.84, 1.07) * mm, "end": v(1.81, 1.1) * mm});
            skLineSegment(sketch, "E712", {"start": v(1.81, 1.1) * mm, "end": v(1.79, 1.14) * mm});
            skLineSegment(sketch, "E713", {"start": v(1.79, 1.14) * mm, "end": v(1.76, 1.18) * mm});
            skLineSegment(sketch, "E714", {"start": v(1.76, 1.18) * mm, "end": v(1.74, 1.21) * mm});
            skLineSegment(sketch, "E715", {"start": v(1.74, 1.21) * mm, "end": v(1.7, 1.24) * mm});
            skLineSegment(sketch, "E716", {"start": v(1.7, 1.24) * mm, "end": v(1.67, 1.27) * mm});
            skLineSegment(sketch, "E717", {"start": v(1.67, 1.27) * mm, "end": v(1.64, 1.3) * mm});
            skLineSegment(sketch, "E718", {"start": v(1.64, 1.3) * mm, "end": v(1.6, 1.32) * mm});
            skLineSegment(sketch, "E719", {"start": v(1.6, 1.32) * mm, "end": v(1.57, 1.34) * mm});
            skLineSegment(sketch, "E720", {"start": v(1.57, 1.34) * mm, "end": v(1.53, 1.36) * mm});
            skLineSegment(sketch, "E721", {"start": v(1.53, 1.36) * mm, "end": v(1.49, 1.38) * mm});
            skLineSegment(sketch, "E722", {"start": v(1.49, 1.38) * mm, "end": v(1.45, 1.4) * mm});
            skLineSegment(sketch, "E723", {"start": v(1.45, 1.4) * mm, "end": v(1.4, 1.41) * mm});
            skLineSegment(sketch, "E724", {"start": v(1.4, 1.41) * mm, "end": v(1.36, 1.42) * mm});
            skLineSegment(sketch, "E725", {"start": v(1.36, 1.42) * mm, "end": v(1.3, 1.43) * mm});
            skLineSegment(sketch, "E726", {"start": v(1.3, 1.43) * mm, "end": v(1.26, 1.44) * mm});
            skLineSegment(sketch, "E727", {"start": v(1.26, 1.44) * mm, "end": v(1.2, 1.44) * mm});
            skLineSegment(sketch, "E728", {"start": v(1.2, 1.44) * mm, "end": v(1.15, 1.45) * mm});
            skLineSegment(sketch, "E729", {"start": v(1.15, 1.45) * mm, "end": v(1.1, 1.45) * mm});
            skLineSegment(sketch, "E730", {"start": v(1.1, 1.45) * mm, "end": v(1.04, 1.45) * mm});
            skLineSegment(sketch, "E731", {"start": v(1.04, 1.45) * mm, "end": v(0.98, 1.44) * mm});
            skLineSegment(sketch, "E732", {"start": v(0.98, 1.44) * mm, "end": v(0.92, 1.43) * mm});
            skLineSegment(sketch, "E733", {"start": v(0.92, 1.43) * mm, "end": v(0.86, 1.42) * mm});
            skLineSegment(sketch, "E734", {"start": v(0.86, 1.42) * mm, "end": v(0.8, 1.4) * mm});
            skLineSegment(sketch, "E735", {"start": v(0.8, 1.4) * mm, "end": v(0.73, 1.38) * mm});
            skLineSegment(sketch, "E736", {"start": v(0.73, 1.38) * mm, "end": v(0.67, 1.36) * mm});
            skLineSegment(sketch, "E737", {"start": v(0.67, 1.36) * mm, "end": v(0.6, 1.33) * mm});
            skLineSegment(sketch, "E738", {"start": v(0.6, 1.33) * mm, "end": v(0.46, 1.27) * mm});
            skLineSegment(sketch, "E739", {"start": v(0.46, 1.27) * mm, "end": v(0.32, 1.2) * mm});
            skLineSegment(sketch, "E740", {"start": v(0.32, 1.2) * mm, "end": v(0.18, 1.1) * mm});
            skLineSegment(sketch, "E741", {"start": v(0.18, 1.1) * mm, "end": v(0.04, 1.01) * mm});
            skLineSegment(sketch, "E742", {"start": v(0.04, 1.01) * mm, "end": v(-0.1, 0.91) * mm});
            skLineSegment(sketch, "E743", {"start": v(-0.1, 0.91) * mm, "end": v(-0.24, 0.8) * mm});
            skLineSegment(sketch, "E744", {"start": v(-0.24, 0.8) * mm, "end": v(-0.38, 0.68) * mm});
            skLineSegment(sketch, "E745", {"start": v(-0.38, 0.68) * mm, "end": v(-0.52, 0.56) * mm});
            skLineSegment(sketch, "E746", {"start": v(-0.52, 0.56) * mm, "end": v(-0.66, 0.42) * mm});
            skLineSegment(sketch, "E747", {"start": v(-0.66, 0.42) * mm, "end": v(-0.9, 0.15) * mm});
            skLineSegment(sketch, "E748", {"start": v(-0.9, 0.15) * mm, "end": v(-1.03, 0) * mm});
            skLineSegment(sketch, "E749", {"start": v(-1.03, 0) * mm, "end": v(-1.13, -0.14) * mm});
            skLineSegment(sketch, "E750", {"start": v(-1.13, -0.14) * mm, "end": v(-1.23, -0.3) * mm});
            skLineSegment(sketch, "E751", {"start": v(-1.23, -0.3) * mm, "end": v(-1.32, -0.44) * mm});
            skLineSegment(sketch, "E752", {"start": v(-1.32, -0.44) * mm, "end": v(-1.4, -0.6) * mm});
            skLineSegment(sketch, "E753", {"start": v(-1.4, -0.6) * mm, "end": v(-1.48, -0.75) * mm});
            skLineSegment(sketch, "E754", {"start": v(-1.48, -0.75) * mm, "end": v(-1.53, -0.9) * mm});
            skLineSegment(sketch, "E755", {"start": v(-1.53, -0.9) * mm, "end": v(-1.56, -0.97) * mm});
            skLineSegment(sketch, "E756", {"start": v(-1.56, -0.97) * mm, "end": v(-1.58, -1.04) * mm});
            skLineSegment(sketch, "E757", {"start": v(-1.58, -1.04) * mm, "end": v(-1.6, -1.12) * mm});
            skLineSegment(sketch, "E758", {"start": v(-1.6, -1.12) * mm, "end": v(-1.6, -1.19) * mm});
            skLineSegment(sketch, "E759", {"start": v(-1.6, -1.19) * mm, "end": v(-2.57, -6.77) * mm});
            skLineSegment(sketch, "E760", {"start": v(-2.57, -6.77) * mm, "end": v(-4.18, -6.77) * mm});
            skLineSegment(sketch, "E761", {"start": v(-4.18, -6.77) * mm, "end": v(-2.7, 1.66) * mm});
            skLineSegment(sketch, "E762", {"start": v(-2.7, 1.66) * mm, "end": v(-3.84, 1.9) * mm});
            skLineSegment(sketch, "E763", {"start": v(-3.84, 1.9) * mm, "end": v(-3.76, 2.34) * mm});
            skLineSegment(sketch, "E764", {"start": v(-3.76, 2.34) * mm, "end": v(-1.07, 2.34) * mm});
            skLineSegment(sketch, "E765", {"start": v(-1.07, 2.34) * mm, "end": v(-1.34, 0.46) * mm});
            skLineSegment(sketch, "E766", {"start": v(-1.34, 0.46) * mm, "end": v(-1.17, 0.68) * mm});
            skLineSegment(sketch, "E767", {"start": v(-1.17, 0.68) * mm, "end": v(-0.82, 1.1) * mm});
            skLineSegment(sketch, "E768", {"start": v(-0.82, 1.1) * mm, "end": v(-0.64, 1.3) * mm});
            skLineSegment(sketch, "E769", {"start": v(-0.64, 1.3) * mm, "end": v(-0.45, 1.5) * mm});
            skLineSegment(sketch, "E770", {"start": v(-0.45, 1.5) * mm, "end": v(-0.25, 1.66) * mm});
            skLineSegment(sketch, "E771", {"start": v(-0.25, 1.66) * mm, "end": v(-0.06, 1.82) * mm});
            skLineSegment(sketch, "E772", {"start": v(-0.06, 1.82) * mm, "end": v(0.15, 1.97) * mm});
            skLineSegment(sketch, "E773", {"start": v(0.15, 1.97) * mm, "end": v(0.35, 2.1) * mm});
            skLineSegment(sketch, "E774", {"start": v(0.35, 2.1) * mm, "end": v(0.55, 2.23) * mm});
            skLineSegment(sketch, "E775", {"start": v(0.55, 2.23) * mm, "end": v(0.76, 2.33) * mm});
            skLineSegment(sketch, "E776", {"start": v(0.76, 2.33) * mm, "end": v(0.96, 2.42) * mm});
            skLineSegment(sketch, "E777", {"start": v(0.96, 2.42) * mm, "end": v(1.06, 2.46) * mm});
            skLineSegment(sketch, "E778", {"start": v(1.06, 2.46) * mm, "end": v(1.17, 2.49) * mm});
            skLineSegment(sketch, "E779", {"start": v(1.17, 2.49) * mm, "end": v(1.27, 2.52) * mm});
            skLineSegment(sketch, "E780", {"start": v(1.27, 2.52) * mm, "end": v(1.37, 2.54) * mm});
            skLineSegment(sketch, "E781", {"start": v(1.37, 2.54) * mm, "end": v(1.47, 2.56) * mm});
            skLineSegment(sketch, "E782", {"start": v(1.47, 2.56) * mm, "end": v(1.57, 2.57) * mm});
            skLineSegment(sketch, "E783", {"start": v(1.57, 2.57) * mm, "end": v(1.67, 2.58) * mm});
            skLineSegment(sketch, "E784", {"start": v(1.67, 2.58) * mm, "end": v(1.77, 2.58) * mm});
            skLineSegment(sketch, "E785", {"start": v(1.77, 2.58) * mm, "end": v(1.88, 2.58) * mm});
            skLineSegment(sketch, "E786", {"start": v(1.88, 2.58) * mm, "end": v(1.98, 2.57) * mm});
            skLineSegment(sketch, "E787", {"start": v(1.98, 2.57) * mm, "end": v(2.08, 2.56) * mm});
            skLineSegment(sketch, "E788", {"start": v(2.08, 2.56) * mm, "end": v(2.18, 2.55) * mm});
            skLineSegment(sketch, "E789", {"start": v(2.18, 2.55) * mm, "end": v(2.27, 2.53) * mm});
            skLineSegment(sketch, "E790", {"start": v(2.27, 2.53) * mm, "end": v(2.36, 2.5) * mm});
            skLineSegment(sketch, "E791", {"start": v(2.36, 2.5) * mm, "end": v(2.44, 2.48) * mm});
            skLineSegment(sketch, "E792", {"start": v(2.44, 2.48) * mm, "end": v(2.53, 2.45) * mm});
            skLineSegment(sketch, "E793", {"start": v(2.53, 2.45) * mm, "end": v(2.6, 2.41) * mm});
            skLineSegment(sketch, "E794", {"start": v(2.6, 2.41) * mm, "end": v(2.69, 2.37) * mm});
            skLineSegment(sketch, "E795", {"start": v(2.69, 2.37) * mm, "end": v(2.76, 2.33) * mm});
            skLineSegment(sketch, "E796", {"start": v(2.76, 2.33) * mm, "end": v(2.83, 2.28) * mm});
            skLineSegment(sketch, "E797", {"start": v(2.83, 2.28) * mm, "end": v(2.9, 2.22) * mm});
            skLineSegment(sketch, "E798", {"start": v(2.9, 2.22) * mm, "end": v(2.97, 2.17) * mm});
            skLineSegment(sketch, "E799", {"start": v(2.97, 2.17) * mm, "end": v(3.03, 2.1) * mm});
            skLineSegment(sketch, "E800", {"start": v(3.03, 2.1) * mm, "end": v(3.1, 2.04) * mm});
            skLineSegment(sketch, "E801", {"start": v(3.1, 2.04) * mm, "end": v(3.15, 1.97) * mm});
            skLineSegment(sketch, "E802", {"start": v(3.15, 1.97) * mm, "end": v(3.2, 1.9) * mm});
            skLineSegment(sketch, "E803", {"start": v(3.2, 1.9) * mm, "end": v(3.25, 1.82) * mm});
            skLineSegment(sketch, "E804", {"start": v(3.25, 1.82) * mm, "end": v(3.3, 1.74) * mm});
            skLineSegment(sketch, "E805", {"start": v(3.3, 1.74) * mm, "end": v(3.34, 1.66) * mm});
            skLineSegment(sketch, "E806", {"start": v(3.34, 1.66) * mm, "end": v(3.38, 1.57) * mm});
            skLineSegment(sketch, "E807", {"start": v(3.38, 1.57) * mm, "end": v(3.42, 1.47) * mm});
            skLineSegment(sketch, "E808", {"start": v(3.42, 1.47) * mm, "end": v(3.45, 1.38) * mm});
            skLineSegment(sketch, "E809", {"start": v(3.45, 1.38) * mm, "end": v(3.47, 1.28) * mm});
            skLineSegment(sketch, "E810", {"start": v(3.47, 1.28) * mm, "end": v(3.5, 1.17) * mm});
            skLineSegment(sketch, "E811", {"start": v(3.5, 1.17) * mm, "end": v(3.52, 1.06) * mm});
            skLineSegment(sketch, "E812", {"start": v(3.52, 1.06) * mm, "end": v(3.54, 0.95) * mm});
            skLineSegment(sketch, "E813", {"start": v(3.54, 0.95) * mm, "end": v(3.55, 0.83) * mm});
            skLineSegment(sketch, "E814", {"start": v(3.55, 0.83) * mm, "end": v(3.56, 0.71) * mm});
            skLineSegment(sketch, "E815", {"start": v(3.56, 0.71) * mm, "end": v(3.57, 0.46) * mm});
            skLineSegment(sketch, "E816", {"start": v(12.1, -4.9) * mm, "end": v(12.1, -5) * mm});
            skLineSegment(sketch, "E817", {"start": v(12.1, -5) * mm, "end": v(12.1, -5.06) * mm});
            skLineSegment(sketch, "E818", {"start": v(12.1, -5.06) * mm, "end": v(12.12, -5.1) * mm});
            skLineSegment(sketch, "E819", {"start": v(12.12, -5.1) * mm, "end": v(12.12, -5.15) * mm});
            skLineSegment(sketch, "E820", {"start": v(12.12, -5.15) * mm, "end": v(12.13, -5.2) * mm});
            skLineSegment(sketch, "E821", {"start": v(12.13, -5.2) * mm, "end": v(12.15, -5.25) * mm});
            skLineSegment(sketch, "E822", {"start": v(12.15, -5.25) * mm, "end": v(12.16, -5.3) * mm});
            skLineSegment(sketch, "E823", {"start": v(12.16, -5.3) * mm, "end": v(12.18, -5.34) * mm});
            skLineSegment(sketch, "E824", {"start": v(12.18, -5.34) * mm, "end": v(12.2, -5.38) * mm});
            skLineSegment(sketch, "E825", {"start": v(12.2, -5.38) * mm, "end": v(12.21, -5.42) * mm});
            skLineSegment(sketch, "E826", {"start": v(12.21, -5.42) * mm, "end": v(12.23, -5.46) * mm});
            skLineSegment(sketch, "E827", {"start": v(12.23, -5.46) * mm, "end": v(12.25, -5.5) * mm});
            skLineSegment(sketch, "E828", {"start": v(12.25, -5.5) * mm, "end": v(12.28, -5.53) * mm});
            skLineSegment(sketch, "E829", {"start": v(12.28, -5.53) * mm, "end": v(12.3, -5.57) * mm});
            skLineSegment(sketch, "E830", {"start": v(12.3, -5.57) * mm, "end": v(12.33, -5.6) * mm});
            skLineSegment(sketch, "E831", {"start": v(12.33, -5.6) * mm, "end": v(12.36, -5.64) * mm});
            skLineSegment(sketch, "E832", {"start": v(12.36, -5.64) * mm, "end": v(12.4, -5.67) * mm});
            skLineSegment(sketch, "E833", {"start": v(12.4, -5.67) * mm, "end": v(12.43, -5.7) * mm});
            skLineSegment(sketch, "E834", {"start": v(12.43, -5.7) * mm, "end": v(12.47, -5.72) * mm});
            skLineSegment(sketch, "E835", {"start": v(12.47, -5.72) * mm, "end": v(12.5, -5.75) * mm});
            skLineSegment(sketch, "E836", {"start": v(12.5, -5.75) * mm, "end": v(12.55, -5.77) * mm});
            skLineSegment(sketch, "E837", {"start": v(12.55, -5.77) * mm, "end": v(12.59, -5.8) * mm});
            skLineSegment(sketch, "E838", {"start": v(12.59, -5.8) * mm, "end": v(12.63, -5.8) * mm});
            skLineSegment(sketch, "E839", {"start": v(12.63, -5.8) * mm, "end": v(12.68, -5.82) * mm});
            skLineSegment(sketch, "E840", {"start": v(12.68, -5.82) * mm, "end": v(12.73, -5.84) * mm});
            skLineSegment(sketch, "E841", {"start": v(12.73, -5.84) * mm, "end": v(12.78, -5.85) * mm});
            skLineSegment(sketch, "E842", {"start": v(12.78, -5.85) * mm, "end": v(12.84, -5.86) * mm});
            skLineSegment(sketch, "E843", {"start": v(12.84, -5.86) * mm, "end": v(12.9, -5.87) * mm});
            skLineSegment(sketch, "E844", {"start": v(12.9, -5.87) * mm, "end": v(12.95, -5.87) * mm});
            skLineSegment(sketch, "E845", {"start": v(12.95, -5.87) * mm, "end": v(13, -5.88) * mm});
            skLineSegment(sketch, "E846", {"start": v(13, -5.88) * mm, "end": v(13.07, -5.88) * mm});
            skLineSegment(sketch, "E847", {"start": v(13.07, -5.88) * mm, "end": v(13.17, -5.87) * mm});
            skLineSegment(sketch, "E848", {"start": v(13.17, -5.87) * mm, "end": v(13.28, -5.86) * mm});
            skLineSegment(sketch, "E849", {"start": v(13.28, -5.86) * mm, "end": v(13.38, -5.85) * mm});
            skLineSegment(sketch, "E850", {"start": v(13.38, -5.85) * mm, "end": v(13.48, -5.83) * mm});
            skLineSegment(sketch, "E851", {"start": v(13.48, -5.83) * mm, "end": v(13.59, -5.8) * mm});
            skLineSegment(sketch, "E852", {"start": v(13.59, -5.8) * mm, "end": v(13.7, -5.77) * mm});
            skLineSegment(sketch, "E853", {"start": v(13.7, -5.77) * mm, "end": v(13.8, -5.74) * mm});
            skLineSegment(sketch, "E854", {"start": v(13.8, -5.74) * mm, "end": v(13.9, -5.7) * mm});
            skLineSegment(sketch, "E855", {"start": v(13.9, -5.7) * mm, "end": v(14.11, -5.6) * mm});
            skLineSegment(sketch, "E856", {"start": v(14.11, -5.6) * mm, "end": v(14.32, -5.48) * mm});
            skLineSegment(sketch, "E857", {"start": v(14.32, -5.48) * mm, "end": v(14.52, -5.36) * mm});
            skLineSegment(sketch, "E858", {"start": v(14.52, -5.36) * mm, "end": v(14.72, -5.22) * mm});
            skLineSegment(sketch, "E859", {"start": v(14.72, -5.22) * mm, "end": v(14.91, -5.06) * mm});
            skLineSegment(sketch, "E860", {"start": v(14.91, -5.06) * mm, "end": v(15.1, -4.9) * mm});
            skLineSegment(sketch, "E861", {"start": v(15.1, -4.9) * mm, "end": v(15.28, -4.72) * mm});
            skLineSegment(sketch, "E862", {"start": v(15.28, -4.72) * mm, "end": v(15.45, -4.54) * mm});
            skLineSegment(sketch, "E863", {"start": v(15.45, -4.54) * mm, "end": v(15.62, -4.35) * mm});
            skLineSegment(sketch, "E864", {"start": v(15.62, -4.35) * mm, "end": v(15.77, -4.16) * mm});
            skLineSegment(sketch, "E865", {"start": v(15.77, -4.16) * mm, "end": v(15.9, -3.97) * mm});
            skLineSegment(sketch, "E866", {"start": v(15.9, -3.97) * mm, "end": v(16.03, -3.78) * mm});
            skLineSegment(sketch, "E867", {"start": v(16.03, -3.78) * mm, "end": v(17.1, 2.34) * mm});
            skLineSegment(sketch, "E868", {"start": v(17.1, 2.34) * mm, "end": v(18.7, 2.34) * mm});
            skLineSegment(sketch, "E869", {"start": v(18.7, 2.34) * mm, "end": v(17.23, -6.09) * mm});
            skLineSegment(sketch, "E870", {"start": v(17.23, -6.09) * mm, "end": v(18.37, -6.33) * mm});
            skLineSegment(sketch, "E871", {"start": v(18.37, -6.33) * mm, "end": v(18.3, -6.77) * mm});
            skLineSegment(sketch, "E872", {"start": v(18.3, -6.77) * mm, "end": v(15.6, -6.77) * mm});
            skLineSegment(sketch, "E873", {"start": v(15.6, -6.77) * mm, "end": v(15.86, -4.9) * mm});
            skLineSegment(sketch, "E874", {"start": v(15.86, -4.9) * mm, "end": v(15.67, -5.13) * mm});
            skLineSegment(sketch, "E875", {"start": v(15.67, -5.13) * mm, "end": v(15.29, -5.56) * mm});
            skLineSegment(sketch, "E876", {"start": v(15.29, -5.56) * mm, "end": v(15.09, -5.76) * mm});
            skLineSegment(sketch, "E877", {"start": v(15.09, -5.76) * mm, "end": v(14.88, -5.95) * mm});
            skLineSegment(sketch, "E878", {"start": v(14.88, -5.95) * mm, "end": v(14.68, -6.12) * mm});
            skLineSegment(sketch, "E879", {"start": v(14.68, -6.12) * mm, "end": v(14.47, -6.28) * mm});
            skLineSegment(sketch, "E880", {"start": v(14.47, -6.28) * mm, "end": v(14.25, -6.43) * mm});
            skLineSegment(sketch, "E881", {"start": v(14.25, -6.43) * mm, "end": v(14.04, -6.56) * mm});
            skLineSegment(sketch, "E882", {"start": v(14.04, -6.56) * mm, "end": v(13.82, -6.67) * mm});
            skLineSegment(sketch, "E883", {"start": v(13.82, -6.67) * mm, "end": v(13.6, -6.76) * mm});
            skLineSegment(sketch, "E884", {"start": v(13.6, -6.76) * mm, "end": v(13.37, -6.84) * mm});
            skLineSegment(sketch, "E885", {"start": v(13.37, -6.84) * mm, "end": v(13.15, -6.91) * mm});
            skLineSegment(sketch, "E886", {"start": v(13.15, -6.91) * mm, "end": v(12.92, -6.96) * mm});
            skLineSegment(sketch, "E887", {"start": v(12.92, -6.96) * mm, "end": v(12.7, -7) * mm});
            skLineSegment(sketch, "E888", {"start": v(12.7, -7) * mm, "end": v(12.46, -7) * mm});
            skLineSegment(sketch, "E889", {"start": v(12.46, -7) * mm, "end": v(12.24, -7) * mm});
            skLineSegment(sketch, "E890", {"start": v(12.24, -7) * mm, "end": v(12.03, -6.97) * mm});
            skLineSegment(sketch, "E891", {"start": v(12.03, -6.97) * mm, "end": v(11.84, -6.93) * mm});
            skLineSegment(sketch, "E892", {"start": v(11.84, -6.93) * mm, "end": v(11.74, -6.91) * mm});
            skLineSegment(sketch, "E893", {"start": v(11.74, -6.91) * mm, "end": v(11.65, -6.88) * mm});
            skLineSegment(sketch, "E894", {"start": v(11.65, -6.88) * mm, "end": v(11.56, -6.85) * mm});
            skLineSegment(sketch, "E895", {"start": v(11.56, -6.85) * mm, "end": v(11.47, -6.82) * mm});
            skLineSegment(sketch, "E896", {"start": v(11.47, -6.82) * mm, "end": v(11.4, -6.78) * mm});
            skLineSegment(sketch, "E897", {"start": v(11.4, -6.78) * mm, "end": v(11.31, -6.73) * mm});
            skLineSegment(sketch, "E898", {"start": v(11.31, -6.73) * mm, "end": v(11.24, -6.69) * mm});
            skLineSegment(sketch, "E899", {"start": v(11.24, -6.69) * mm, "end": v(11.16, -6.63) * mm});
            skLineSegment(sketch, "E900", {"start": v(11.16, -6.63) * mm, "end": v(11.1, -6.58) * mm});
            skLineSegment(sketch, "E901", {"start": v(11.1, -6.58) * mm, "end": v(11.03, -6.52) * mm});
            skLineSegment(sketch, "E902", {"start": v(11.03, -6.52) * mm, "end": v(10.96, -6.45) * mm});
            skLineSegment(sketch, "E903", {"start": v(10.96, -6.45) * mm, "end": v(10.9, -6.38) * mm});
            skLineSegment(sketch, "E904", {"start": v(10.9, -6.38) * mm, "end": v(10.85, -6.3) * mm});
            skLineSegment(sketch, "E905", {"start": v(10.85, -6.3) * mm, "end": v(10.8, -6.23) * mm});
            skLineSegment(sketch, "E906", {"start": v(10.8, -6.23) * mm, "end": v(10.75, -6.15) * mm});
            skLineSegment(sketch, "E907", {"start": v(10.75, -6.15) * mm, "end": v(10.7, -6.07) * mm});
            skLineSegment(sketch, "E908", {"start": v(10.7, -6.07) * mm, "end": v(10.67, -5.98) * mm});
            skLineSegment(sketch, "E909", {"start": v(10.67, -5.98) * mm, "end": v(10.63, -5.89) * mm});
            skLineSegment(sketch, "E910", {"start": v(10.63, -5.89) * mm, "end": v(10.6, -5.79) * mm});
            skLineSegment(sketch, "E911", {"start": v(10.6, -5.79) * mm, "end": v(10.57, -5.68) * mm});
            skLineSegment(sketch, "E912", {"start": v(10.57, -5.68) * mm, "end": v(10.55, -5.57) * mm});
            skLineSegment(sketch, "E913", {"start": v(10.55, -5.57) * mm, "end": v(10.53, -5.46) * mm});
            skLineSegment(sketch, "E914", {"start": v(10.53, -5.46) * mm, "end": v(10.51, -5.34) * mm});
            skLineSegment(sketch, "E915", {"start": v(10.51, -5.34) * mm, "end": v(10.5, -5.22) * mm});
            skLineSegment(sketch, "E916", {"start": v(10.5, -5.22) * mm, "end": v(10.5, -5.09) * mm});
            skLineSegment(sketch, "E917", {"start": v(10.5, -5.09) * mm, "end": v(10.5, -4.96) * mm});
            skLineSegment(sketch, "E918", {"start": v(10.5, -4.96) * mm, "end": v(10.5, -4.93) * mm});
            skLineSegment(sketch, "E919", {"start": v(10.5, -4.93) * mm, "end": v(10.5, -4.9) * mm});
            skLineSegment(sketch, "E920", {"start": v(10.5, -4.9) * mm, "end": v(10.5, -4.86) * mm});
            skLineSegment(sketch, "E921", {"start": v(10.5, -4.86) * mm, "end": v(10.5, -4.82) * mm});
            skLineSegment(sketch, "E922", {"start": v(10.5, -4.82) * mm, "end": v(10.5, -4.78) * mm});
            skLineSegment(sketch, "E923", {"start": v(10.5, -4.78) * mm, "end": v(10.5, -4.74) * mm});
            skLineSegment(sketch, "E924", {"start": v(10.5, -4.74) * mm, "end": v(10.5, -4.7) * mm});
            skLineSegment(sketch, "E925", {"start": v(10.5, -4.7) * mm, "end": v(10.51, -4.65) * mm});
            skLineSegment(sketch, "E926", {"start": v(10.51, -4.65) * mm, "end": v(10.53, -4.55) * mm});
            skLineSegment(sketch, "E927", {"start": v(10.53, -4.55) * mm, "end": v(10.54, -4.44) * mm});
            skLineSegment(sketch, "E928", {"start": v(10.54, -4.44) * mm, "end": v(10.57, -4.22) * mm});
            skLineSegment(sketch, "E929", {"start": v(10.57, -4.22) * mm, "end": v(10.6, -4.1) * mm});
            skLineSegment(sketch, "E930", {"start": v(10.6, -4.1) * mm, "end": v(10.63, -3.87) * mm});
            skLineSegment(sketch, "E931", {"start": v(10.63, -3.87) * mm, "end": v(10.65, -3.74) * mm});
            skLineSegment(sketch, "E932", {"start": v(10.65, -3.74) * mm, "end": v(10.67, -3.62) * mm});
            skLineSegment(sketch, "E933", {"start": v(10.67, -3.62) * mm, "end": v(10.72, -3.38) * mm});
            skLineSegment(sketch, "E934", {"start": v(10.72, -3.38) * mm, "end": v(10.74, -3.27) * mm});
            skLineSegment(sketch, "E935", {"start": v(10.74, -3.27) * mm, "end": v(11.59, 1.67) * mm});
            skLineSegment(sketch, "E936", {"start": v(11.59, 1.67) * mm, "end": v(10.51, 1.9) * mm});
            skLineSegment(sketch, "E937", {"start": v(10.51, 1.9) * mm, "end": v(10.6, 2.34) * mm});
            skLineSegment(sketch, "E938", {"start": v(10.6, 2.34) * mm, "end": v(13.31, 2.34) * mm});
            skLineSegment(sketch, "E939", {"start": v(13.31, 2.34) * mm, "end": v(12.32, -3.29) * mm});
            skLineSegment(sketch, "E940", {"start": v(12.32, -3.29) * mm, "end": v(12.3, -3.4) * mm});
            skLineSegment(sketch, "E941", {"start": v(12.3, -3.4) * mm, "end": v(12.27, -3.62) * mm});
            skLineSegment(sketch, "E942", {"start": v(12.27, -3.62) * mm, "end": v(12.25, -3.73) * mm});
            skLineSegment(sketch, "E943", {"start": v(12.25, -3.73) * mm, "end": v(12.23, -3.85) * mm});
            skLineSegment(sketch, "E944", {"start": v(12.23, -3.85) * mm, "end": v(12.19, -4.08) * mm});
            skLineSegment(sketch, "E945", {"start": v(12.19, -4.08) * mm, "end": v(12.17, -4.2) * mm});
            skLineSegment(sketch, "E946", {"start": v(12.17, -4.2) * mm, "end": v(12.16, -4.3) * mm});
            skLineSegment(sketch, "E947", {"start": v(12.16, -4.3) * mm, "end": v(12.14, -4.4) * mm});
            skLineSegment(sketch, "E948", {"start": v(12.14, -4.4) * mm, "end": v(12.13, -4.5) * mm});
            skLineSegment(sketch, "E949", {"start": v(12.13, -4.5) * mm, "end": v(12.12, -4.6) * mm});
            skLineSegment(sketch, "E950", {"start": v(12.12, -4.6) * mm, "end": v(12.12, -4.64) * mm});
            skLineSegment(sketch, "E951", {"start": v(12.12, -4.64) * mm, "end": v(12.11, -4.69) * mm});
            skLineSegment(sketch, "E952", {"start": v(12.11, -4.69) * mm, "end": v(12.1, -4.73) * mm});
            skLineSegment(sketch, "E953", {"start": v(12.1, -4.73) * mm, "end": v(12.1, -4.76) * mm});
            skLineSegment(sketch, "E954", {"start": v(12.1, -4.76) * mm, "end": v(12.1, -4.8) * mm});
            skLineSegment(sketch, "E955", {"start": v(12.1, -4.8) * mm, "end": v(12.1, -4.84) * mm});
            skLineSegment(sketch, "E956", {"start": v(12.1, -4.84) * mm, "end": v(12.1, -4.87) * mm});
            skLineSegment(sketch, "E957", {"start": v(12.1, -4.87) * mm, "end": v(12.1, -4.9) * mm});
            skLineSegment(sketch, "E958", {"start": v(26.93, 0.48) * mm, "end": v(26.92, 0.59) * mm});
            skLineSegment(sketch, "E959", {"start": v(26.92, 0.59) * mm, "end": v(26.92, 0.64) * mm});
            skLineSegment(sketch, "E960", {"start": v(26.92, 0.64) * mm, "end": v(26.91, 0.69) * mm});
            skLineSegment(sketch, "E961", {"start": v(26.91, 0.69) * mm, "end": v(26.9, 0.74) * mm});
            skLineSegment(sketch, "E962", {"start": v(26.9, 0.74) * mm, "end": v(26.9, 0.78) * mm});
            skLineSegment(sketch, "E963", {"start": v(26.9, 0.78) * mm, "end": v(26.88, 0.83) * mm});
            skLineSegment(sketch, "E964", {"start": v(26.88, 0.83) * mm, "end": v(26.87, 0.87) * mm});
            skLineSegment(sketch, "E965", {"start": v(26.87, 0.87) * mm, "end": v(26.85, 0.92) * mm});
            skLineSegment(sketch, "E966", {"start": v(26.85, 0.92) * mm, "end": v(26.83, 0.96) * mm});
            skLineSegment(sketch, "E967", {"start": v(26.83, 0.96) * mm, "end": v(26.82, 1) * mm});
            skLineSegment(sketch, "E968", {"start": v(26.82, 1) * mm, "end": v(26.8, 1.04) * mm});
            skLineSegment(sketch, "E969", {"start": v(26.8, 1.04) * mm, "end": v(26.77, 1.08) * mm});
            skLineSegment(sketch, "E970", {"start": v(26.77, 1.08) * mm, "end": v(26.75, 1.12) * mm});
            skLineSegment(sketch, "E971", {"start": v(26.75, 1.12) * mm, "end": v(26.72, 1.15) * mm});
            skLineSegment(sketch, "E972", {"start": v(26.72, 1.15) * mm, "end": v(26.7, 1.19) * mm});
            skLineSegment(sketch, "E973", {"start": v(26.7, 1.19) * mm, "end": v(26.66, 1.22) * mm});
            skLineSegment(sketch, "E974", {"start": v(26.66, 1.22) * mm, "end": v(26.63, 1.25) * mm});
            skLineSegment(sketch, "E975", {"start": v(26.63, 1.25) * mm, "end": v(26.6, 1.28) * mm});
            skLineSegment(sketch, "E976", {"start": v(26.6, 1.28) * mm, "end": v(26.56, 1.3) * mm});
            skLineSegment(sketch, "E977", {"start": v(26.56, 1.3) * mm, "end": v(26.52, 1.33) * mm});
            skLineSegment(sketch, "E978", {"start": v(26.52, 1.33) * mm, "end": v(26.48, 1.35) * mm});
            skLineSegment(sketch, "E979", {"start": v(26.48, 1.35) * mm, "end": v(26.44, 1.37) * mm});
            skLineSegment(sketch, "E980", {"start": v(26.44, 1.37) * mm, "end": v(26.4, 1.4) * mm});
            skLineSegment(sketch, "E981", {"start": v(26.4, 1.4) * mm, "end": v(26.35, 1.4) * mm});
            skLineSegment(sketch, "E982", {"start": v(26.35, 1.4) * mm, "end": v(26.3, 1.42) * mm});
            skLineSegment(sketch, "E983", {"start": v(26.3, 1.42) * mm, "end": v(26.25, 1.43) * mm});
            skLineSegment(sketch, "E984", {"start": v(26.25, 1.43) * mm, "end": v(26.2, 1.44) * mm});
            skLineSegment(sketch, "E985", {"start": v(26.2, 1.44) * mm, "end": v(26.14, 1.45) * mm});
            skLineSegment(sketch, "E986", {"start": v(26.14, 1.45) * mm, "end": v(26.08, 1.45) * mm});
            skLineSegment(sketch, "E987", {"start": v(26.08, 1.45) * mm, "end": v(26.02, 1.46) * mm});
            skLineSegment(sketch, "E988", {"start": v(26.02, 1.46) * mm, "end": v(25.96, 1.46) * mm});
            skLineSegment(sketch, "E989", {"start": v(25.96, 1.46) * mm, "end": v(25.85, 1.46) * mm});
            skLineSegment(sketch, "E990", {"start": v(25.85, 1.46) * mm, "end": v(25.75, 1.45) * mm});
            skLineSegment(sketch, "E991", {"start": v(25.75, 1.45) * mm, "end": v(25.65, 1.43) * mm});
            skLineSegment(sketch, "E992", {"start": v(25.65, 1.43) * mm, "end": v(25.54, 1.4) * mm});
            skLineSegment(sketch, "E993", {"start": v(25.54, 1.4) * mm, "end": v(25.44, 1.38) * mm});
            skLineSegment(sketch, "E994", {"start": v(25.44, 1.38) * mm, "end": v(25.34, 1.35) * mm});
            skLineSegment(sketch, "E995", {"start": v(25.34, 1.35) * mm, "end": v(25.23, 1.3) * mm});
            skLineSegment(sketch, "E996", {"start": v(25.23, 1.3) * mm, "end": v(25.12, 1.26) * mm});
            skLineSegment(sketch, "E997", {"start": v(25.12, 1.26) * mm, "end": v(24.91, 1.17) * mm});
            skLineSegment(sketch, "E998", {"start": v(24.91, 1.17) * mm, "end": v(24.7, 1.05) * mm});
            skLineSegment(sketch, "E999", {"start": v(24.7, 1.05) * mm, "end": v(24.5, 0.92) * mm});
            skLineSegment(sketch, "E1000", {"start": v(24.5, 0.92) * mm, "end": v(24.3, 0.78) * mm});
            skLineSegment(sketch, "E1001", {"start": v(24.3, 0.78) * mm, "end": v(24.1, 0.62) * mm});
            skLineSegment(sketch, "E1002", {"start": v(24.1, 0.62) * mm, "end": v(23.92, 0.46) * mm});
            skLineSegment(sketch, "E1003", {"start": v(23.92, 0.46) * mm, "end": v(23.74, 0.28) * mm});
            skLineSegment(sketch, "E1004", {"start": v(23.74, 0.28) * mm, "end": v(23.56, 0.1) * mm});
            skLineSegment(sketch, "E1005", {"start": v(23.56, 0.1) * mm, "end": v(23.4, -0.1) * mm});
            skLineSegment(sketch, "E1006", {"start": v(23.4, -0.1) * mm, "end": v(23.25, -0.29) * mm});
            skLineSegment(sketch, "E1007", {"start": v(23.25, -0.29) * mm, "end": v(23.11, -0.47) * mm});
            skLineSegment(sketch, "E1008", {"start": v(23.11, -0.47) * mm, "end": v(23, -0.66) * mm});
            skLineSegment(sketch, "E1009", {"start": v(23, -0.66) * mm, "end": v(21.93, -6.77) * mm});
            skLineSegment(sketch, "E1010", {"start": v(21.93, -6.77) * mm, "end": v(20.32, -6.77) * mm});
            skLineSegment(sketch, "E1011", {"start": v(20.32, -6.77) * mm, "end": v(21.8, 1.67) * mm});
            skLineSegment(sketch, "E1012", {"start": v(21.8, 1.67) * mm, "end": v(20.66, 1.91) * mm});
            skLineSegment(sketch, "E1013", {"start": v(20.66, 1.91) * mm, "end": v(20.73, 2.35) * mm});
            skLineSegment(sketch, "E1014", {"start": v(20.73, 2.35) * mm, "end": v(23.43, 2.35) * mm});
            skLineSegment(sketch, "E1015", {"start": v(23.43, 2.35) * mm, "end": v(23.17, 0.49) * mm});
            skLineSegment(sketch, "E1016", {"start": v(23.17, 0.49) * mm, "end": v(23.35, 0.72) * mm});
            skLineSegment(sketch, "E1017", {"start": v(23.35, 0.72) * mm, "end": v(23.73, 1.15) * mm});
            skLineSegment(sketch, "E1018", {"start": v(23.73, 1.15) * mm, "end": v(23.93, 1.35) * mm});
            skLineSegment(sketch, "E1019", {"start": v(23.93, 1.35) * mm, "end": v(24.14, 1.54) * mm});
            skLineSegment(sketch, "E1020", {"start": v(24.14, 1.54) * mm, "end": v(24.34, 1.7) * mm});
            skLineSegment(sketch, "E1021", {"start": v(24.34, 1.7) * mm, "end": v(24.55, 1.87) * mm});
            skLineSegment(sketch, "E1022", {"start": v(24.55, 1.87) * mm, "end": v(24.76, 2.01) * mm});
            skLineSegment(sketch, "E1023", {"start": v(24.76, 2.01) * mm, "end": v(24.98, 2.14) * mm});
            skLineSegment(sketch, "E1024", {"start": v(24.98, 2.14) * mm, "end": v(25.2, 2.25) * mm});
            skLineSegment(sketch, "E1025", {"start": v(25.2, 2.25) * mm, "end": v(25.42, 2.35) * mm});
            skLineSegment(sketch, "E1026", {"start": v(25.42, 2.35) * mm, "end": v(25.65, 2.43) * mm});
            skLineSegment(sketch, "E1027", {"start": v(25.65, 2.43) * mm, "end": v(25.87, 2.5) * mm});
            skLineSegment(sketch, "E1028", {"start": v(25.87, 2.5) * mm, "end": v(26.1, 2.54) * mm});
            skLineSegment(sketch, "E1029", {"start": v(26.1, 2.54) * mm, "end": v(26.34, 2.57) * mm});
            skLineSegment(sketch, "E1030", {"start": v(26.34, 2.57) * mm, "end": v(26.57, 2.58) * mm});
            skLineSegment(sketch, "E1031", {"start": v(26.57, 2.58) * mm, "end": v(26.78, 2.57) * mm});
            skLineSegment(sketch, "E1032", {"start": v(26.78, 2.57) * mm, "end": v(26.89, 2.57) * mm});
            skLineSegment(sketch, "E1033", {"start": v(26.89, 2.57) * mm, "end": v(27, 2.55) * mm});
            skLineSegment(sketch, "E1034", {"start": v(27, 2.55) * mm, "end": v(27.1, 2.54) * mm});
            skLineSegment(sketch, "E1035", {"start": v(27.1, 2.54) * mm, "end": v(27.19, 2.52) * mm});
            skLineSegment(sketch, "E1036", {"start": v(27.19, 2.52) * mm, "end": v(27.28, 2.5) * mm});
            skLineSegment(sketch, "E1037", {"start": v(27.28, 2.5) * mm, "end": v(27.37, 2.47) * mm});
            skLineSegment(sketch, "E1038", {"start": v(27.37, 2.47) * mm, "end": v(27.46, 2.43) * mm});
            skLineSegment(sketch, "E1039", {"start": v(27.46, 2.43) * mm, "end": v(27.55, 2.4) * mm});
            skLineSegment(sketch, "E1040", {"start": v(27.55, 2.4) * mm, "end": v(27.63, 2.36) * mm});
            skLineSegment(sketch, "E1041", {"start": v(27.63, 2.36) * mm, "end": v(27.71, 2.32) * mm});
            skLineSegment(sketch, "E1042", {"start": v(27.71, 2.32) * mm, "end": v(27.79, 2.27) * mm});
            skLineSegment(sketch, "E1043", {"start": v(27.79, 2.27) * mm, "end": v(27.86, 2.21) * mm});
            skLineSegment(sketch, "E1044", {"start": v(27.86, 2.21) * mm, "end": v(27.93, 2.16) * mm});
            skLineSegment(sketch, "E1045", {"start": v(27.93, 2.16) * mm, "end": v(28, 2.1) * mm});
            skLineSegment(sketch, "E1046", {"start": v(28, 2.1) * mm, "end": v(28.05, 2.03) * mm});
            skLineSegment(sketch, "E1047", {"start": v(28.05, 2.03) * mm, "end": v(28.11, 1.96) * mm});
            skLineSegment(sketch, "E1048", {"start": v(28.11, 1.96) * mm, "end": v(28.17, 1.89) * mm});
            skLineSegment(sketch, "E1049", {"start": v(28.17, 1.89) * mm, "end": v(28.22, 1.81) * mm});
            skLineSegment(sketch, "E1050", {"start": v(28.22, 1.81) * mm, "end": v(28.27, 1.73) * mm});
            skLineSegment(sketch, "E1051", {"start": v(28.27, 1.73) * mm, "end": v(28.31, 1.64) * mm});
            skLineSegment(sketch, "E1052", {"start": v(28.31, 1.64) * mm, "end": v(28.35, 1.55) * mm});
            skLineSegment(sketch, "E1053", {"start": v(28.35, 1.55) * mm, "end": v(28.39, 1.46) * mm});
            skLineSegment(sketch, "E1054", {"start": v(28.39, 1.46) * mm, "end": v(28.42, 1.36) * mm});
            skLineSegment(sketch, "E1055", {"start": v(28.42, 1.36) * mm, "end": v(28.45, 1.26) * mm});
            skLineSegment(sketch, "E1056", {"start": v(28.45, 1.26) * mm, "end": v(28.48, 1.15) * mm});
            skLineSegment(sketch, "E1057", {"start": v(28.48, 1.15) * mm, "end": v(28.5, 1.03) * mm});
            skLineSegment(sketch, "E1058", {"start": v(28.5, 1.03) * mm, "end": v(28.51, 0.92) * mm});
            skLineSegment(sketch, "E1059", {"start": v(28.51, 0.92) * mm, "end": v(28.52, 0.8) * mm});
            skLineSegment(sketch, "E1060", {"start": v(28.52, 0.8) * mm, "end": v(28.53, 0.67) * mm});
            skLineSegment(sketch, "E1061", {"start": v(28.53, 0.67) * mm, "end": v(28.53, 0.54) * mm});
            skLineSegment(sketch, "E1062", {"start": v(28.53, 0.54) * mm, "end": v(28.53, 0.52) * mm});
            skLineSegment(sketch, "E1063", {"start": v(28.53, 0.52) * mm, "end": v(28.53, 0.5) * mm});
            skLineSegment(sketch, "E1064", {"start": v(28.53, 0.5) * mm, "end": v(28.53, 0.47) * mm});
            skLineSegment(sketch, "E1065", {"start": v(28.53, 0.47) * mm, "end": v(28.53, 0.44) * mm});
            skLineSegment(sketch, "E1066", {"start": v(28.53, 0.44) * mm, "end": v(28.53, 0.4) * mm});
            skLineSegment(sketch, "E1067", {"start": v(28.53, 0.4) * mm, "end": v(28.52, 0.36) * mm});
            skLineSegment(sketch, "E1068", {"start": v(28.52, 0.36) * mm, "end": v(28.52, 0.31) * mm});
            skLineSegment(sketch, "E1069", {"start": v(28.52, 0.31) * mm, "end": v(28.51, 0.27) * mm});
            skLineSegment(sketch, "E1070", {"start": v(28.51, 0.27) * mm, "end": v(28.5, 0.22) * mm});
            skLineSegment(sketch, "E1071", {"start": v(28.5, 0.22) * mm, "end": v(28.5, 0.12) * mm});
            skLineSegment(sketch, "E1072", {"start": v(28.5, 0.12) * mm, "end": v(28.48, 0.01) * mm});
            skLineSegment(sketch, "E1073", {"start": v(28.48, 0.01) * mm, "end": v(28.46, -0.1) * mm});
            skLineSegment(sketch, "E1074", {"start": v(28.46, -0.1) * mm, "end": v(28.45, -0.2) * mm});
            skLineSegment(sketch, "E1075", {"start": v(28.45, -0.2) * mm, "end": v(28.43, -0.33) * mm});
            skLineSegment(sketch, "E1076", {"start": v(28.43, -0.33) * mm, "end": v(28.39, -0.57) * mm});
            skLineSegment(sketch, "E1077", {"start": v(28.39, -0.57) * mm, "end": v(28.37, -0.7) * mm});
            skLineSegment(sketch, "E1078", {"start": v(28.37, -0.7) * mm, "end": v(28.35, -0.81) * mm});
            skLineSegment(sketch, "E1079", {"start": v(28.35, -0.81) * mm, "end": v(28.31, -1.04) * mm});
            skLineSegment(sketch, "E1080", {"start": v(28.31, -1.04) * mm, "end": v(28.3, -1.15) * mm});
            skLineSegment(sketch, "E1081", {"start": v(28.3, -1.15) * mm, "end": v(27.44, -6.1) * mm});
            skLineSegment(sketch, "E1082", {"start": v(27.44, -6.1) * mm, "end": v(28.7, -6.33) * mm});
            skLineSegment(sketch, "E1083", {"start": v(28.7, -6.33) * mm, "end": v(28.63, -6.77) * mm});
            skLineSegment(sketch, "E1084", {"start": v(28.63, -6.77) * mm, "end": v(25.71, -6.77) * mm});
            skLineSegment(sketch, "E1085", {"start": v(25.71, -6.77) * mm, "end": v(26.7, -1.13) * mm});
            skLineSegment(sketch, "E1086", {"start": v(26.7, -1.13) * mm, "end": v(26.72, -1.02) * mm});
            skLineSegment(sketch, "E1087", {"start": v(26.72, -1.02) * mm, "end": v(26.76, -0.8) * mm});
            skLineSegment(sketch, "E1088", {"start": v(26.76, -0.8) * mm, "end": v(26.78, -0.68) * mm});
            skLineSegment(sketch, "E1089", {"start": v(26.78, -0.68) * mm, "end": v(26.8, -0.57) * mm});
            skLineSegment(sketch, "E1090", {"start": v(26.8, -0.57) * mm, "end": v(26.83, -0.34) * mm});
            skLineSegment(sketch, "E1091", {"start": v(26.83, -0.34) * mm, "end": v(26.85, -0.23) * mm});
            skLineSegment(sketch, "E1092", {"start": v(26.85, -0.23) * mm, "end": v(26.87, -0.12) * mm});
            skLineSegment(sketch, "E1093", {"start": v(26.87, -0.12) * mm, "end": v(26.88, -0.01) * mm});
            skLineSegment(sketch, "E1094", {"start": v(26.88, -0.01) * mm, "end": v(26.9, 0.08) * mm});
            skLineSegment(sketch, "E1095", {"start": v(26.9, 0.08) * mm, "end": v(26.9, 0.18) * mm});
            skLineSegment(sketch, "E1096", {"start": v(26.9, 0.18) * mm, "end": v(26.91, 0.22) * mm});
            skLineSegment(sketch, "E1097", {"start": v(26.91, 0.22) * mm, "end": v(26.91, 0.27) * mm});
            skLineSegment(sketch, "E1098", {"start": v(26.91, 0.27) * mm, "end": v(26.92, 0.3) * mm});
            skLineSegment(sketch, "E1099", {"start": v(26.92, 0.3) * mm, "end": v(26.92, 0.35) * mm});
            skLineSegment(sketch, "E1100", {"start": v(26.92, 0.35) * mm, "end": v(26.92, 0.38) * mm});
            skLineSegment(sketch, "E1101", {"start": v(26.92, 0.38) * mm, "end": v(26.92, 0.42) * mm});
            skLineSegment(sketch, "E1102", {"start": v(26.92, 0.42) * mm, "end": v(26.93, 0.45) * mm});
            skLineSegment(sketch, "E1103", {"start": v(26.93, 0.45) * mm, "end": v(26.93, 0.48) * mm});
            skLineSegment(sketch, "E1104", {"start": v(37.2, 2.35) * mm, "end": v(37.2, 2.36) * mm});
            skLineSegment(sketch, "E1105", {"start": v(37.2, 2.36) * mm, "end": v(37.2, 2.38) * mm});
            skLineSegment(sketch, "E1106", {"start": v(37.2, 2.38) * mm, "end": v(37.2, 2.4) * mm});
            skLineSegment(sketch, "E1107", {"start": v(37.2, 2.4) * mm, "end": v(37.2, 2.41) * mm});
            skLineSegment(sketch, "E1108", {"start": v(37.2, 2.41) * mm, "end": v(37.2, 2.45) * mm});
            skLineSegment(sketch, "E1109", {"start": v(37.2, 2.45) * mm, "end": v(37.21, 2.49) * mm});
            skLineSegment(sketch, "E1110", {"start": v(37.21, 2.49) * mm, "end": v(37.22, 2.53) * mm});
            skLineSegment(sketch, "E1111", {"start": v(37.22, 2.53) * mm, "end": v(37.22, 2.58) * mm});
            skLineSegment(sketch, "E1112", {"start": v(37.22, 2.58) * mm, "end": v(37.23, 2.63) * mm});
            skLineSegment(sketch, "E1113", {"start": v(37.23, 2.63) * mm, "end": v(37.23, 2.68) * mm});
            skLineSegment(sketch, "E1114", {"start": v(37.23, 2.68) * mm, "end": v(37.25, 2.8) * mm});
            skLineSegment(sketch, "E1115", {"start": v(37.25, 2.8) * mm, "end": v(37.28, 3.02) * mm});
            skLineSegment(sketch, "E1116", {"start": v(37.28, 3.02) * mm, "end": v(37.3, 3.13) * mm});
            skLineSegment(sketch, "E1117", {"start": v(37.3, 3.13) * mm, "end": v(37.32, 3.25) * mm});
            skLineSegment(sketch, "E1118", {"start": v(37.32, 3.25) * mm, "end": v(37.36, 3.49) * mm});
            skLineSegment(sketch, "E1119", {"start": v(37.36, 3.49) * mm, "end": v(37.37, 3.6) * mm});
            skLineSegment(sketch, "E1120", {"start": v(37.37, 3.6) * mm, "end": v(37.38, 3.65) * mm});
            skLineSegment(sketch, "E1121", {"start": v(37.38, 3.65) * mm, "end": v(37.39, 3.7) * mm});
            skLineSegment(sketch, "E1122", {"start": v(37.39, 3.7) * mm, "end": v(37.4, 3.76) * mm});
            skLineSegment(sketch, "E1123", {"start": v(37.4, 3.76) * mm, "end": v(37.4, 3.8) * mm});
            skLineSegment(sketch, "E1124", {"start": v(37.4, 3.8) * mm, "end": v(37.41, 3.85) * mm});
            skLineSegment(sketch, "E1125", {"start": v(37.41, 3.85) * mm, "end": v(37.42, 3.89) * mm});
            skLineSegment(sketch, "E1126", {"start": v(37.42, 3.89) * mm, "end": v(37.43, 3.93) * mm});
            skLineSegment(sketch, "E1127", {"start": v(37.43, 3.93) * mm, "end": v(37.44, 3.97) * mm});
            skLineSegment(sketch, "E1128", {"start": v(37.44, 3.97) * mm, "end": v(37.85, 6.33) * mm});
            skLineSegment(sketch, "E1129", {"start": v(37.85, 6.33) * mm, "end": v(36.36, 6.56) * mm});
            skLineSegment(sketch, "E1130", {"start": v(36.36, 6.56) * mm, "end": v(36.44, 7) * mm});
            skLineSegment(sketch, "E1131", {"start": v(36.44, 7) * mm, "end": v(39.58, 7) * mm});
            skLineSegment(sketch, "E1132", {"start": v(39.58, 7) * mm, "end": v(37.25, -6.09) * mm});
            skLineSegment(sketch, "E1133", {"start": v(37.25, -6.09) * mm, "end": v(38.35, -6.33) * mm});
            skLineSegment(sketch, "E1134", {"start": v(38.35, -6.33) * mm, "end": v(38.27, -6.77) * mm});
            skLineSegment(sketch, "E1135", {"start": v(38.27, -6.77) * mm, "end": v(35.51, -6.77) * mm});
            skLineSegment(sketch, "E1136", {"start": v(35.51, -6.77) * mm, "end": v(35.8, -5.26) * mm});
            skLineSegment(sketch, "E1137", {"start": v(35.8, -5.26) * mm, "end": v(35.59, -5.46) * mm});
            skLineSegment(sketch, "E1138", {"start": v(35.59, -5.46) * mm, "end": v(35.39, -5.66) * mm});
            skLineSegment(sketch, "E1139", {"start": v(35.39, -5.66) * mm, "end": v(35.2, -5.84) * mm});
            skLineSegment(sketch, "E1140", {"start": v(35.2, -5.84) * mm, "end": v(35, -6) * mm});
            skLineSegment(sketch, "E1141", {"start": v(35, -6) * mm, "end": v(34.8, -6.16) * mm});
            skLineSegment(sketch, "E1142", {"start": v(34.8, -6.16) * mm, "end": v(34.6, -6.3) * mm});
            skLineSegment(sketch, "E1143", {"start": v(34.6, -6.3) * mm, "end": v(34.42, -6.43) * mm});
            skLineSegment(sketch, "E1144", {"start": v(34.42, -6.43) * mm, "end": v(34.23, -6.54) * mm});
            skLineSegment(sketch, "E1145", {"start": v(34.23, -6.54) * mm, "end": v(34.05, -6.64) * mm});
            skLineSegment(sketch, "E1146", {"start": v(34.05, -6.64) * mm, "end": v(33.86, -6.73) * mm});
            skLineSegment(sketch, "E1147", {"start": v(33.86, -6.73) * mm, "end": v(33.68, -6.8) * mm});
            skLineSegment(sketch, "E1148", {"start": v(33.68, -6.8) * mm, "end": v(33.5, -6.86) * mm});
            skLineSegment(sketch, "E1149", {"start": v(33.5, -6.86) * mm, "end": v(33.32, -6.91) * mm});
            skLineSegment(sketch, "E1150", {"start": v(33.32, -6.91) * mm, "end": v(33.14, -6.94) * mm});
            skLineSegment(sketch, "E1151", {"start": v(33.14, -6.94) * mm, "end": v(32.97, -6.96) * mm});
            skLineSegment(sketch, "E1152", {"start": v(32.97, -6.96) * mm, "end": v(32.8, -6.97) * mm});
            skLineSegment(sketch, "E1153", {"start": v(32.8, -6.97) * mm, "end": v(32.65, -6.97) * mm});
            skLineSegment(sketch, "E1154", {"start": v(32.65, -6.97) * mm, "end": v(32.51, -6.96) * mm});
            skLineSegment(sketch, "E1155", {"start": v(32.51, -6.96) * mm, "end": v(32.38, -6.94) * mm});
            skLineSegment(sketch, "E1156", {"start": v(32.38, -6.94) * mm, "end": v(32.24, -6.92) * mm});
            skLineSegment(sketch, "E1157", {"start": v(32.24, -6.92) * mm, "end": v(32.11, -6.88) * mm});
            skLineSegment(sketch, "E1158", {"start": v(32.11, -6.88) * mm, "end": v(31.99, -6.85) * mm});
            skLineSegment(sketch, "E1159", {"start": v(31.99, -6.85) * mm, "end": v(31.86, -6.8) * mm});
            skLineSegment(sketch, "E1160", {"start": v(31.86, -6.8) * mm, "end": v(31.74, -6.75) * mm});
            skLineSegment(sketch, "E1161", {"start": v(31.74, -6.75) * mm, "end": v(31.62, -6.69) * mm});
            skLineSegment(sketch, "E1162", {"start": v(31.62, -6.69) * mm, "end": v(31.51, -6.62) * mm});
            skLineSegment(sketch, "E1163", {"start": v(31.51, -6.62) * mm, "end": v(31.4, -6.55) * mm});
            skLineSegment(sketch, "E1164", {"start": v(31.4, -6.55) * mm, "end": v(31.3, -6.48) * mm});
            skLineSegment(sketch, "E1165", {"start": v(31.3, -6.48) * mm, "end": v(31.2, -6.4) * mm});
            skLineSegment(sketch, "E1166", {"start": v(31.2, -6.4) * mm, "end": v(31.1, -6.3) * mm});
            skLineSegment(sketch, "E1167", {"start": v(31.1, -6.3) * mm, "end": v(31.01, -6.2) * mm});
            skLineSegment(sketch, "E1168", {"start": v(31.01, -6.2) * mm, "end": v(30.93, -6.1) * mm});
            skLineSegment(sketch, "E1169", {"start": v(30.93, -6.1) * mm, "end": v(30.84, -6) * mm});
            skLineSegment(sketch, "E1170", {"start": v(30.84, -6) * mm, "end": v(30.77, -5.88) * mm});
            skLineSegment(sketch, "E1171", {"start": v(30.77, -5.88) * mm, "end": v(30.7, -5.76) * mm});
            skLineSegment(sketch, "E1172", {"start": v(30.7, -5.76) * mm, "end": v(30.62, -5.64) * mm});
            skLineSegment(sketch, "E1173", {"start": v(30.62, -5.64) * mm, "end": v(30.56, -5.5) * mm});
            skLineSegment(sketch, "E1174", {"start": v(30.56, -5.5) * mm, "end": v(30.5, -5.37) * mm});
            skLineSegment(sketch, "E1175", {"start": v(30.5, -5.37) * mm, "end": v(30.45, -5.22) * mm});
            skLineSegment(sketch, "E1176", {"start": v(30.45, -5.22) * mm, "end": v(30.4, -5.07) * mm});
            skLineSegment(sketch, "E1177", {"start": v(30.4, -5.07) * mm, "end": v(30.35, -4.92) * mm});
            skLineSegment(sketch, "E1178", {"start": v(30.35, -4.92) * mm, "end": v(30.31, -4.76) * mm});
            skLineSegment(sketch, "E1179", {"start": v(30.31, -4.76) * mm, "end": v(30.28, -4.6) * mm});
            skLineSegment(sketch, "E1180", {"start": v(30.28, -4.6) * mm, "end": v(30.24, -4.25) * mm});
            skLineSegment(sketch, "E1181", {"start": v(30.24, -4.25) * mm, "end": v(30.21, -3.89) * mm});
            skLineSegment(sketch, "E1182", {"start": v(30.21, -3.89) * mm, "end": v(30.21, -3.7) * mm});
            skLineSegment(sketch, "E1183", {"start": v(30.21, -3.7) * mm, "end": v(30.22, -3.28) * mm});
            skLineSegment(sketch, "E1184", {"start": v(30.22, -3.28) * mm, "end": v(30.26, -2.88) * mm});
            skLineSegment(sketch, "E1185", {"start": v(30.26, -2.88) * mm, "end": v(30.31, -2.47) * mm});
            skLineSegment(sketch, "E1186", {"start": v(30.31, -2.47) * mm, "end": v(30.4, -2.08) * mm});
            skLineSegment(sketch, "E1187", {"start": v(30.4, -2.08) * mm, "end": v(30.5, -1.69) * mm});
            skLineSegment(sketch, "E1188", {"start": v(30.5, -1.69) * mm, "end": v(30.62, -1.3) * mm});
            skLineSegment(sketch, "E1189", {"start": v(30.62, -1.3) * mm, "end": v(30.76, -0.94) * mm});
            skLineSegment(sketch, "E1190", {"start": v(30.76, -0.94) * mm, "end": v(30.92, -0.59) * mm});
            skLineSegment(sketch, "E1191", {"start": v(30.92, -0.59) * mm, "end": v(31.1, -0.25) * mm});
            skLineSegment(sketch, "E1192", {"start": v(31.1, -0.25) * mm, "end": v(31.3, 0.08) * mm});
            skLineSegment(sketch, "E1193", {"start": v(31.3, 0.08) * mm, "end": v(31.5, 0.39) * mm});
            skLineSegment(sketch, "E1194", {"start": v(31.5, 0.39) * mm, "end": v(31.73, 0.68) * mm});
            skLineSegment(sketch, "E1195", {"start": v(31.73, 0.68) * mm, "end": v(31.98, 0.96) * mm});
            skLineSegment(sketch, "E1196", {"start": v(31.98, 0.96) * mm, "end": v(32.25, 1.22) * mm});
            skLineSegment(sketch, "E1197", {"start": v(32.25, 1.22) * mm, "end": v(32.52, 1.46) * mm});
            skLineSegment(sketch, "E1198", {"start": v(32.52, 1.46) * mm, "end": v(32.82, 1.68) * mm});
            skLineSegment(sketch, "E1199", {"start": v(32.82, 1.68) * mm, "end": v(33.12, 1.88) * mm});
            skLineSegment(sketch, "E1200", {"start": v(33.12, 1.88) * mm, "end": v(33.44, 2.06) * mm});
            skLineSegment(sketch, "E1201", {"start": v(33.44, 2.06) * mm, "end": v(33.77, 2.21) * mm});
            skLineSegment(sketch, "E1202", {"start": v(33.77, 2.21) * mm, "end": v(34.12, 2.34) * mm});
            skLineSegment(sketch, "E1203", {"start": v(34.12, 2.34) * mm, "end": v(34.47, 2.44) * mm});
            skLineSegment(sketch, "E1204", {"start": v(34.47, 2.44) * mm, "end": v(34.84, 2.51) * mm});
            skLineSegment(sketch, "E1205", {"start": v(34.84, 2.51) * mm, "end": v(35.21, 2.56) * mm});
            skLineSegment(sketch, "E1206", {"start": v(35.21, 2.56) * mm, "end": v(35.6, 2.57) * mm});
            skLineSegment(sketch, "E1207", {"start": v(35.6, 2.57) * mm, "end": v(35.83, 2.57) * mm});
            skLineSegment(sketch, "E1208", {"start": v(35.83, 2.57) * mm, "end": v(36.06, 2.56) * mm});
            skLineSegment(sketch, "E1209", {"start": v(36.06, 2.56) * mm, "end": v(36.27, 2.54) * mm});
            skLineSegment(sketch, "E1210", {"start": v(36.27, 2.54) * mm, "end": v(36.47, 2.51) * mm});
            skLineSegment(sketch, "E1211", {"start": v(36.47, 2.51) * mm, "end": v(36.66, 2.48) * mm});
            skLineSegment(sketch, "E1212", {"start": v(36.66, 2.48) * mm, "end": v(36.85, 2.44) * mm});
            skLineSegment(sketch, "E1213", {"start": v(36.85, 2.44) * mm, "end": v(37.03, 2.4) * mm});
            skLineSegment(sketch, "E1214", {"start": v(37.03, 2.4) * mm, "end": v(37.2, 2.35) * mm});
            skLineSegment(sketch, "E1215", {"start": v(36.97, 1.34) * mm, "end": v(36.8, 1.45) * mm});
            skLineSegment(sketch, "E1216", {"start": v(36.8, 1.45) * mm, "end": v(36.63, 1.54) * mm});
            skLineSegment(sketch, "E1217", {"start": v(36.63, 1.54) * mm, "end": v(36.45, 1.62) * mm});
            skLineSegment(sketch, "E1218", {"start": v(36.45, 1.62) * mm, "end": v(36.28, 1.7) * mm});
            skLineSegment(sketch, "E1219", {"start": v(36.28, 1.7) * mm, "end": v(36.18, 1.72) * mm});
            skLineSegment(sketch, "E1220", {"start": v(36.18, 1.72) * mm, "end": v(36.09, 1.75) * mm});
            skLineSegment(sketch, "E1221", {"start": v(36.09, 1.75) * mm, "end": v(35.98, 1.77) * mm});
            skLineSegment(sketch, "E1222", {"start": v(35.98, 1.77) * mm, "end": v(35.88, 1.79) * mm});
            skLineSegment(sketch, "E1223", {"start": v(35.88, 1.79) * mm, "end": v(35.77, 1.8) * mm});
            skLineSegment(sketch, "E1224", {"start": v(35.77, 1.8) * mm, "end": v(35.65, 1.8) * mm});
            skLineSegment(sketch, "E1225", {"start": v(35.65, 1.8) * mm, "end": v(35.53, 1.81) * mm});
            skLineSegment(sketch, "E1226", {"start": v(35.53, 1.81) * mm, "end": v(35.4, 1.82) * mm});
            skLineSegment(sketch, "E1227", {"start": v(35.4, 1.82) * mm, "end": v(35.27, 1.81) * mm});
            skLineSegment(sketch, "E1228", {"start": v(35.27, 1.81) * mm, "end": v(35.15, 1.8) * mm});
            skLineSegment(sketch, "E1229", {"start": v(35.15, 1.8) * mm, "end": v(35.02, 1.79) * mm});
            skLineSegment(sketch, "E1230", {"start": v(35.02, 1.79) * mm, "end": v(34.9, 1.76) * mm});
            skLineSegment(sketch, "E1231", {"start": v(34.9, 1.76) * mm, "end": v(34.78, 1.73) * mm});
            skLineSegment(sketch, "E1232", {"start": v(34.78, 1.73) * mm, "end": v(34.66, 1.7) * mm});
            skLineSegment(sketch, "E1233", {"start": v(34.66, 1.7) * mm, "end": v(34.54, 1.65) * mm});
            skLineSegment(sketch, "E1234", {"start": v(34.54, 1.65) * mm, "end": v(34.43, 1.6) * mm});
            skLineSegment(sketch, "E1235", {"start": v(34.43, 1.6) * mm, "end": v(34.31, 1.54) * mm});
            skLineSegment(sketch, "E1236", {"start": v(34.31, 1.54) * mm, "end": v(34.1, 1.4) * mm});
            skLineSegment(sketch, "E1237", {"start": v(34.1, 1.4) * mm, "end": v(33.88, 1.25) * mm});
            skLineSegment(sketch, "E1238", {"start": v(33.88, 1.25) * mm, "end": v(33.68, 1.08) * mm});
            skLineSegment(sketch, "E1239", {"start": v(33.68, 1.08) * mm, "end": v(33.58, 0.98) * mm});
            skLineSegment(sketch, "E1240", {"start": v(33.58, 0.98) * mm, "end": v(33.4, 0.79) * mm});
            skLineSegment(sketch, "E1241", {"start": v(33.4, 0.79) * mm, "end": v(33.21, 0.57) * mm});
            skLineSegment(sketch, "E1242", {"start": v(33.21, 0.57) * mm, "end": v(33.04, 0.34) * mm});
            skLineSegment(sketch, "E1243", {"start": v(33.04, 0.34) * mm, "end": v(32.88, 0.1) * mm});
            skLineSegment(sketch, "E1244", {"start": v(32.88, 0.1) * mm, "end": v(32.74, -0.17) * mm});
            skLineSegment(sketch, "E1245", {"start": v(32.74, -0.17) * mm, "end": v(32.6, -0.44) * mm});
            skLineSegment(sketch, "E1246", {"start": v(32.6, -0.44) * mm, "end": v(32.48, -0.72) * mm});
            skLineSegment(sketch, "E1247", {"start": v(32.48, -0.72) * mm, "end": v(32.37, -1.01) * mm});
            skLineSegment(sketch, "E1248", {"start": v(32.37, -1.01) * mm, "end": v(32.27, -1.31) * mm});
            skLineSegment(sketch, "E1249", {"start": v(32.27, -1.31) * mm, "end": v(32.1, -1.92) * mm});
            skLineSegment(sketch, "E1250", {"start": v(32.1, -1.92) * mm, "end": v(32.04, -2.23) * mm});
            skLineSegment(sketch, "E1251", {"start": v(32.04, -2.23) * mm, "end": v(32, -2.55) * mm});
            skLineSegment(sketch, "E1252", {"start": v(32, -2.55) * mm, "end": v(31.94, -3.17) * mm});
            skLineSegment(sketch, "E1253", {"start": v(31.94, -3.17) * mm, "end": v(31.93, -3.48) * mm});
            skLineSegment(sketch, "E1254", {"start": v(31.93, -3.48) * mm, "end": v(31.94, -3.63) * mm});
            skLineSegment(sketch, "E1255", {"start": v(31.94, -3.63) * mm, "end": v(31.94, -3.78) * mm});
            skLineSegment(sketch, "E1256", {"start": v(31.94, -3.78) * mm, "end": v(31.95, -3.92) * mm});
            skLineSegment(sketch, "E1257", {"start": v(31.95, -3.92) * mm, "end": v(31.97, -4.05) * mm});
            skLineSegment(sketch, "E1258", {"start": v(31.97, -4.05) * mm, "end": v(31.99, -4.18) * mm});
            skLineSegment(sketch, "E1259", {"start": v(31.99, -4.18) * mm, "end": v(32.01, -4.3) * mm});
            skLineSegment(sketch, "E1260", {"start": v(32.01, -4.3) * mm, "end": v(32.04, -4.42) * mm});
            skLineSegment(sketch, "E1261", {"start": v(32.04, -4.42) * mm, "end": v(32.07, -4.53) * mm});
            skLineSegment(sketch, "E1262", {"start": v(32.07, -4.53) * mm, "end": v(32.1, -4.63) * mm});
            skLineSegment(sketch, "E1263", {"start": v(32.1, -4.63) * mm, "end": v(32.14, -4.73) * mm});
            skLineSegment(sketch, "E1264", {"start": v(32.14, -4.73) * mm, "end": v(32.18, -4.83) * mm});
            skLineSegment(sketch, "E1265", {"start": v(32.18, -4.83) * mm, "end": v(32.23, -4.92) * mm});
            skLineSegment(sketch, "E1266", {"start": v(32.23, -4.92) * mm, "end": v(32.27, -5) * mm});
            skLineSegment(sketch, "E1267", {"start": v(32.27, -5) * mm, "end": v(32.32, -5.09) * mm});
            skLineSegment(sketch, "E1268", {"start": v(32.32, -5.09) * mm, "end": v(32.37, -5.16) * mm});
            skLineSegment(sketch, "E1269", {"start": v(32.37, -5.16) * mm, "end": v(32.42, -5.24) * mm});
            skLineSegment(sketch, "E1270", {"start": v(32.42, -5.24) * mm, "end": v(32.48, -5.3) * mm});
            skLineSegment(sketch, "E1271", {"start": v(32.48, -5.3) * mm, "end": v(32.53, -5.36) * mm});
            skLineSegment(sketch, "E1272", {"start": v(32.53, -5.36) * mm, "end": v(32.6, -5.42) * mm});
            skLineSegment(sketch, "E1273", {"start": v(32.6, -5.42) * mm, "end": v(32.66, -5.47) * mm});
            skLineSegment(sketch, "E1274", {"start": v(32.66, -5.47) * mm, "end": v(32.72, -5.52) * mm});
            skLineSegment(sketch, "E1275", {"start": v(32.72, -5.52) * mm, "end": v(32.79, -5.56) * mm});
            skLineSegment(sketch, "E1276", {"start": v(32.79, -5.56) * mm, "end": v(32.85, -5.6) * mm});
            skLineSegment(sketch, "E1277", {"start": v(32.85, -5.6) * mm, "end": v(32.92, -5.63) * mm});
            skLineSegment(sketch, "E1278", {"start": v(32.92, -5.63) * mm, "end": v(33, -5.66) * mm});
            skLineSegment(sketch, "E1279", {"start": v(33, -5.66) * mm, "end": v(33.07, -5.69) * mm});
            skLineSegment(sketch, "E1280", {"start": v(33.07, -5.69) * mm, "end": v(33.14, -5.71) * mm});
            skLineSegment(sketch, "E1281", {"start": v(33.14, -5.71) * mm, "end": v(33.22, -5.73) * mm});
            skLineSegment(sketch, "E1282", {"start": v(33.22, -5.73) * mm, "end": v(33.3, -5.74) * mm});
            skLineSegment(sketch, "E1283", {"start": v(33.3, -5.74) * mm, "end": v(33.36, -5.75) * mm});
            skLineSegment(sketch, "E1284", {"start": v(33.36, -5.75) * mm, "end": v(33.44, -5.76) * mm});
            skLineSegment(sketch, "E1285", {"start": v(33.44, -5.76) * mm, "end": v(33.51, -5.76) * mm});
            skLineSegment(sketch, "E1286", {"start": v(33.51, -5.76) * mm, "end": v(33.65, -5.75) * mm});
            skLineSegment(sketch, "E1287", {"start": v(33.65, -5.75) * mm, "end": v(33.8, -5.74) * mm});
            skLineSegment(sketch, "E1288", {"start": v(33.8, -5.74) * mm, "end": v(33.93, -5.71) * mm});
            skLineSegment(sketch, "E1289", {"start": v(33.93, -5.71) * mm, "end": v(34.08, -5.67) * mm});
            skLineSegment(sketch, "E1290", {"start": v(34.08, -5.67) * mm, "end": v(34.23, -5.62) * mm});
            skLineSegment(sketch, "E1291", {"start": v(34.23, -5.62) * mm, "end": v(34.38, -5.56) * mm});
            skLineSegment(sketch, "E1292", {"start": v(34.38, -5.56) * mm, "end": v(34.53, -5.5) * mm});
            skLineSegment(sketch, "E1293", {"start": v(34.53, -5.5) * mm, "end": v(34.69, -5.41) * mm});
            skLineSegment(sketch, "E1294", {"start": v(34.69, -5.41) * mm, "end": v(34.85, -5.32) * mm});
            skLineSegment(sketch, "E1295", {"start": v(34.85, -5.32) * mm, "end": v(35, -5.21) * mm});
            skLineSegment(sketch, "E1296", {"start": v(35, -5.21) * mm, "end": v(35.16, -5.1) * mm});
            skLineSegment(sketch, "E1297", {"start": v(35.16, -5.1) * mm, "end": v(35.31, -4.98) * mm});
            skLineSegment(sketch, "E1298", {"start": v(35.31, -4.98) * mm, "end": v(35.47, -4.85) * mm});
            skLineSegment(sketch, "E1299", {"start": v(35.47, -4.85) * mm, "end": v(35.77, -4.57) * mm});
            skLineSegment(sketch, "E1300", {"start": v(35.77, -4.57) * mm, "end": v(35.92, -4.41) * mm});
            skLineSegment(sketch, "E1301", {"start": v(35.92, -4.41) * mm, "end": v(36.97, 1.34) * mm});
            skSolve(sketch);
        }
        {
            var Q0;
            Q0=makeQuery(id+"F0.imprint","IMPRINT",FACE,{"disambiguationData":[TD([[makeQuery(id+"F0.imprint","IMPRINT",EDGE,{"derivedFrom":sQuery(id+"F0.wireOp",EDGE,"9c274906-66f2-47cc-ba81-bc829715841a")}),-1.0]])]});
            var Q1;
            {var subQ1=sQuery(id+"F0.wireOp",EDGE,"E3");Q1=makeQuery(id+"F0.imprint","IMPRINT",FACE,{"disambiguationData":[TD([[makeQuery(id+"F0.imprint","IMPRINT",EDGE,{"derivedFrom":subQ1}),-1.0]])]});}
            var Q2;
            Q2=makeQuery(id+"F0.imprint","IMPRINT",FACE,{"disambiguationData":[TD([[makeQuery(id+"F0.imprint","IMPRINT",EDGE,{"derivedFrom":sQuery(id+"F0.wireOp",EDGE,"6ab65d4b-20cc-4260-84e2-1f812e6f8199")}),1.0]])]});
            var Q3;
            Q3=makeQuery(id+"F0.imprint","IMPRINT",FACE,{"disambiguationData":[TD([[makeQuery(id+"F0.imprint","IMPRINT",EDGE,{"derivedFrom":sQuery(id+"F0.wireOp",EDGE,"fbc92326-29e4-4a65-8bcc-6a279c66f74b")}),-1.0]])]});
            var Q4;
            Q4=makeQuery(id+"F0.imprint","IMPRINT",FACE,{"disambiguationData":[TD([[makeQuery(id+"F0.imprint","IMPRINT",EDGE,{"derivedFrom":sQuery(id+"F0.wireOp",EDGE,"E1")}),1.0]])]});
            var Q5;
            Q5=makeQuery(id+"F0.imprint","IMPRINT",FACE,{"disambiguationData":[TD([[makeQuery(id+"F0.imprint","IMPRINT",EDGE,{"derivedFrom":sQuery(id+"F0.wireOp",EDGE,"edff43eb-599a-4c31-8809-e4d85603c349")}),-1.0]])]});
            var Q6;
            Q6=makeQuery(id+"F0.imprint","IMPRINT",FACE,{"disambiguationData":[TD([[makeQuery(id+"F0.imprint","IMPRINT",EDGE,{"derivedFrom":sQuery(id+"F0.wireOp",EDGE,"9c1aa12f-a708-4583-be26-2b383a722471")}),1.0]])]});
            var Q7;
            Q7=makeQuery(id+"F0.imprint","IMPRINT",FACE,{"disambiguationData":[TD([[makeQuery(id+"F0.imprint","IMPRINT",EDGE,{"derivedFrom":sQuery(id+"F0.wireOp",EDGE,"d64aa239-00f7-4386-9746-6503c5a989f5")}),-1.0]])]});
            var Q8;
            {var subQ5=sQuery(id+"F0.wireOp",EDGE,"a99f0830-5d0a-4233-9662-b7695eaebfe7");Q8=makeQuery(id+"F0.imprint","IMPRINT",FACE,{"disambiguationData":[TD([[makeQuery(id+"F0.imprint","IMPRINT",EDGE,{"derivedFrom":subQ5}),-1.0]])]});}
            var Q9;
            Q9=makeQuery(id+"F0.imprint","IMPRINT",FACE,{"disambiguationData":[TD([[makeQuery(id+"F0.imprint","IMPRINT",EDGE,{"derivedFrom":sQuery(id+"F0.wireOp",EDGE,"2a4fbe35-dfba-4a85-95bd-e9da396d757a")}),-1.0]])]});
            var Q10;
            Q10=makeQuery(id+"F0.imprint","IMPRINT",FACE,{"disambiguationData":[TD([[makeQuery(id+"F0.imprint","IMPRINT",EDGE,{"derivedFrom":sQuery(id+"F0.wireOp",EDGE,"2a4fbe35-dfba-4a85-95bd-e9da396d757a")}),1.0]])]});
            var Q11;
            Q11=makeQuery(id+"F0.imprint","IMPRINT",FACE,{"disambiguationData":[TD([[makeQuery(id+"F0.imprint","IMPRINT",EDGE,{"derivedFrom":sQuery(id+"F0.wireOp",EDGE,"7aec7717-0c6f-4bae-bb6d-1404d206293c")}),-1.0]])]});
            var Q12;
            Q12=makeQuery(id+"F0.imprint","IMPRINT",FACE,{"disambiguationData":[TD([[makeQuery(id+"F0.imprint","IMPRINT",EDGE,{"derivedFrom":sQuery(id+"F0.wireOp",EDGE,"2e831668-c073-46cd-8cf9-afdbba8640c2")}),-1.0]])]});
            var Q13;
            Q13=makeQuery(id+"F0.imprint","IMPRINT",FACE,{"disambiguationData":[TD([[makeQuery(id+"F0.imprint","IMPRINT",EDGE,{"derivedFrom":sQuery(id+"F0.wireOp",EDGE,"0ff61a9d-bce7-4498-a74a-3b659cdb3a31")}),1.0]])]});
            var Q14;
            Q14=makeQuery(id+"F0.imprint","IMPRINT",FACE,{"disambiguationData":[TD([[makeQuery(id+"F0.imprint","IMPRINT",EDGE,{"derivedFrom":sQuery(id+"F0.wireOp",EDGE,"a042b107-2d44-4470-895e-1f3e02275d71")}),-1.0]])]});
            var Q15;
            Q15=makeQuery(id+"F0.imprint","IMPRINT",FACE,{"disambiguationData":[TD([[makeQuery(id+"F0.imprint","IMPRINT",EDGE,{"derivedFrom":sQuery(id+"F0.wireOp",EDGE,"95c83fbc-b161-4fb0-9650-2e0c3f26e526")}),-1.0]])]});
            var Q16;
            Q16=makeQuery(id+"F0.imprint","IMPRINT",FACE,{"disambiguationData":[TD([[makeQuery(id+"F0.imprint","IMPRINT",EDGE,{"derivedFrom":sQuery(id+"F0.wireOp",EDGE,"b99bc01f-ffcd-4b76-b182-fcdfcf3af48a")}),-1.0]])]});
            var Q17;
            Q17=makeQuery(id+"F0.imprint","IMPRINT",FACE,{"disambiguationData":[TD([[makeQuery(id+"F0.imprint","IMPRINT",EDGE,{"derivedFrom":sQuery(id+"F0.wireOp",EDGE,"695980f6-fe78-45aa-8406-9730c21c461c")}),-1.0]])]});
            var Q18;
            Q18=makeQuery(id+"F0.imprint","IMPRINT",FACE,{"disambiguationData":[TD([[makeQuery(id+"F0.imprint","IMPRINT",EDGE,{"derivedFrom":sQuery(id+"F0.wireOp",EDGE,"8e396e48-0cb7-43f7-9ff5-ea5343fde688")}),-1.0]])]});
            var Q19;
            Q19=makeQuery(id+"F0.imprint","IMPRINT",FACE,{"disambiguationData":[TD([[makeQuery(id+"F0.imprint","IMPRINT",EDGE,{"derivedFrom":sQuery(id+"F0.wireOp",EDGE,"f8601505-93ae-4942-8ee9-6dae2b73583f")}),-1.0]])]});
            var Q20;
            Q20=makeQuery(id+"F0.imprint","IMPRINT",FACE,{"disambiguationData":[TD([[makeQuery(id+"F0.imprint","IMPRINT",EDGE,{"derivedFrom":sQuery(id+"F0.wireOp",EDGE,"328a7c4d-a5ec-4a4b-9363-a6ff0bef3fca")}),1.0]])]});
            var Q21;
            Q21=makeQuery(id+"F0.imprint","IMPRINT",FACE,{"disambiguationData":[TD([[makeQuery(id+"F0.imprint","IMPRINT",EDGE,{"derivedFrom":sQuery(id+"F0.wireOp",EDGE,"1e94215b-109c-49a7-b724-ba8efd773434")}),1.0]])]});
            var Q22;
            Q22=makeQuery(id+"F0.imprint","IMPRINT",FACE,{"disambiguationData":[TD([[makeQuery(id+"F0.imprint","IMPRINT",EDGE,{"derivedFrom":sQuery(id+"F0.wireOp",EDGE,"21f35bfe-fe16-479b-9939-4457bf5feded")}),-1.0]])]});
            var Q23;
            Q23=makeQuery(id+"F0.imprint","IMPRINT",FACE,{"disambiguationData":[TD([[makeQuery(id+"F0.imprint","IMPRINT",EDGE,{"derivedFrom":sQuery(id+"F0.wireOp",EDGE,"E5")}),-1.0]])]});
            var Q24;
            Q24=makeQuery(id+"F0.imprint","IMPRINT",FACE,{"disambiguationData":[TD([[makeQuery(id+"F0.imprint","IMPRINT",EDGE,{"derivedFrom":sQuery(id+"F0.wireOp",EDGE,"E192")}),-1.0]])]});
            var Q25;
            Q25=makeQuery(id+"F0.imprint","IMPRINT",FACE,{"disambiguationData":[TD([[makeQuery(id+"F0.imprint","IMPRINT",EDGE,{"derivedFrom":sQuery(id+"F0.wireOp",EDGE,"E334")}),-1.0]])]});
            var Q26;
            Q26=makeQuery(id+"F0.imprint","IMPRINT",FACE,{"disambiguationData":[TD([[makeQuery(id+"F0.imprint","IMPRINT",EDGE,{"derivedFrom":sQuery(id+"F0.wireOp",EDGE,"E445")}),1.0]])]});
            var Q27;
            Q27=makeQuery(id+"F0.imprint","IMPRINT",FACE,{"disambiguationData":[TD([[makeQuery(id+"F0.imprint","IMPRINT",EDGE,{"derivedFrom":sQuery(id+"F0.wireOp",EDGE,"E816")}),-1.0]])]});
            var Q28;
            Q28=makeQuery(id+"F0.imprint","IMPRINT",FACE,{"disambiguationData":[TD([[makeQuery(id+"F0.imprint","IMPRINT",EDGE,{"derivedFrom":sQuery(id+"F0.wireOp",EDGE,"E958")}),-1.0]])]});
            var Q29;
            Q29=makeQuery(id+"F0.imprint","IMPRINT",FACE,{"disambiguationData":[TD([[makeQuery(id+"F0.imprint","IMPRINT",EDGE,{"derivedFrom":sQuery(id+"F0.wireOp",EDGE,"E1104")}),-1.0]])]});
            var Q30;
            Q30=makeQuery(id+"F0.imprint","IMPRINT",FACE,{"disambiguationData":[TD([[makeQuery(id+"F0.imprint","IMPRINT",EDGE,{"derivedFrom":sQuery(id+"F0.wireOp",EDGE,"E532")}),-1.0]])]});
            var Q31;
            Q31=makeQuery(id+"F0.imprint","IMPRINT",FACE,{"disambiguationData":[TD([[makeQuery(id+"F0.imprint","IMPRINT",EDGE,{"derivedFrom":sQuery(id+"F0.wireOp",EDGE,"E1215")}),1.0]])]});
            extrude(context, id + "F1", {"entities" : qUnion([Q0, Q1, Q2, Q3, Q4, Q5, Q6, Q7, Q8, Q9, Q10, Q11, Q12, Q13, Q14, Q15, Q16, Q17, Q18, Q19, Q20, Q21, Q22, Q23, Q24, Q25, Q26, Q27, Q28, Q29, Q30, Q31]), "oppositeDirection" : true, "depth" : 1.6 * mm, "offsetDistance" : 25 * mm});
        }
        {
            var Q0;
            Q0=makeQuery(id+"F0.imprint","IMPRINT",FACE,{"disambiguationData":[TD([[makeQuery(id+"F0.imprint","IMPRINT",EDGE,{"derivedFrom":sQuery(id+"F0.wireOp",EDGE,"E1")}),1.0]])]});
            extrude(context, id + "F2", {"entities" : qUnion([Q0]), "operationType" : NewBodyOperationType.ADD, "depth" : 1.6 * mm, "offsetDistance" : 25 * mm});
        }
        {
            var Q0;
            Q0=makeQuery(id+"F0.imprint","IMPRINT",FACE,{"disambiguationData":[TD([[makeQuery(id+"F0.imprint","IMPRINT",EDGE,{"derivedFrom":sQuery(id+"F0.wireOp",EDGE,"E192")}),-1.0]])]});
            var Q1;
            Q1=makeQuery(id+"F0.imprint","IMPRINT",FACE,{"disambiguationData":[TD([[makeQuery(id+"F0.imprint","IMPRINT",EDGE,{"derivedFrom":sQuery(id+"F0.wireOp",EDGE,"E334")}),-1.0]])]});
            var Q2;
            Q2=makeQuery(id+"F0.imprint","IMPRINT",FACE,{"disambiguationData":[TD([[makeQuery(id+"F0.imprint","IMPRINT",EDGE,{"derivedFrom":sQuery(id+"F0.wireOp",EDGE,"E532")}),-1.0]])]});
            var Q3;
            Q3=makeQuery(id+"F0.imprint","IMPRINT",FACE,{"disambiguationData":[TD([[makeQuery(id+"F0.imprint","IMPRINT",EDGE,{"derivedFrom":sQuery(id+"F0.wireOp",EDGE,"E816")}),-1.0]])]});
            var Q4;
            Q4=makeQuery(id+"F0.imprint","IMPRINT",FACE,{"disambiguationData":[TD([[makeQuery(id+"F0.imprint","IMPRINT",EDGE,{"derivedFrom":sQuery(id+"F0.wireOp",EDGE,"E958")}),-1.0]])]});
            var Q5;
            Q5=makeQuery(id+"F0.imprint","IMPRINT",FACE,{"disambiguationData":[TD([[makeQuery(id+"F0.imprint","IMPRINT",EDGE,{"derivedFrom":sQuery(id+"F0.wireOp",EDGE,"E1104")}),-1.0]])]});
            var Q6;
            Q6=makeQuery(id+"F0.imprint","IMPRINT",FACE,{"disambiguationData":[TD([[makeQuery(id+"F0.imprint","IMPRINT",EDGE,{"derivedFrom":sQuery(id+"F0.wireOp",EDGE,"E5")}),-1.0]])]});
            extrude(context, id + "F3", {"entities" : qUnion([Q0, Q1, Q2, Q3, Q4, Q5, Q6]), "operationType" : NewBodyOperationType.ADD, "depth" : 1 * mm, "offsetDistance" : 25 * mm});
        }
    });
